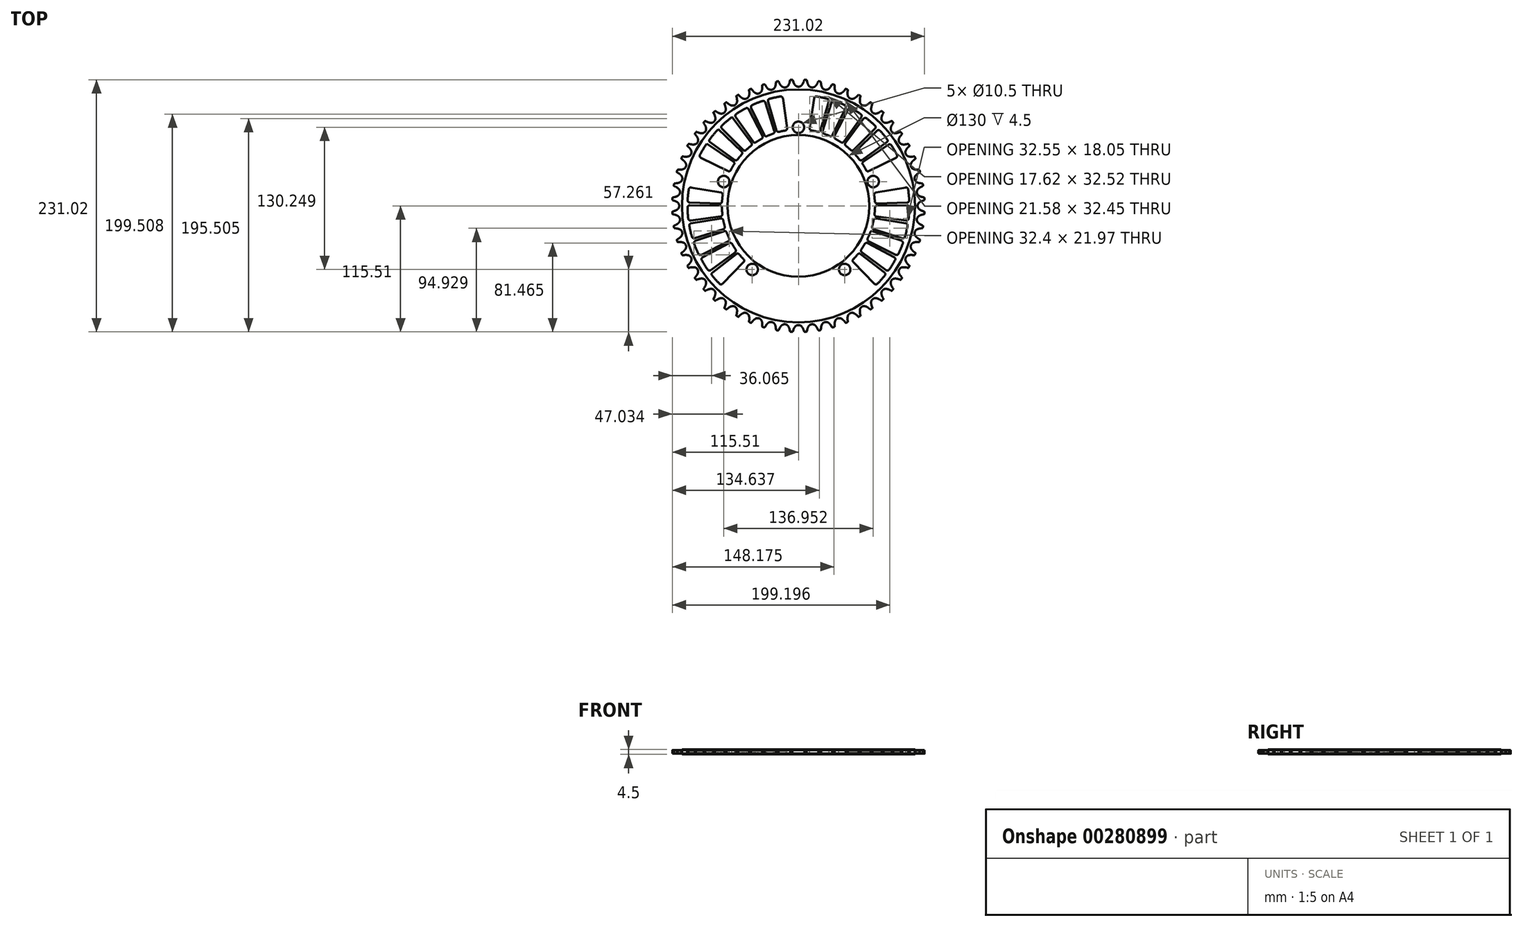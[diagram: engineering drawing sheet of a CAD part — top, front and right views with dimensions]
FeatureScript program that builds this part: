
annotation { "Feature Type Name" : "Feature", "Feature Type Description" : "" }
export const myFeature = defineFeature(function(context is Context, id is Id, definition is map)
    precondition{}
    {
        {
            var Q0;
            Q0=qCreatedBy(makeId("Top.planeOp"),FACE);
            var sketch = newSketch(context, id + "F0", { "sketchPlane" : qUnion([Q0])});
            skArc(sketch, "E0", {"start": v(-3.25, 110.83) * mm, "mid": v(-1.82, 109.61) * mm, "end": v(0, 109.18) * mm});
            skArc(sketch, "E1", {"start": v(-4.68, 113.54) * mm, "mid": v(-4.06, 112.13) * mm, "end": v(-3.25, 110.83) * mm});
            skLineSegment(sketch, "E2", {"start": v(-4.68, 113.54) * mm, "end": v(-5.07, 114.66) * mm});
            skLineSegment(sketch, "E3", {"start": v(-11.11, 112.64) * mm, "end": v(-11.11, 112.57) * mm});
            skArc(sketch, "E4.trimOffspring", {"start": v(-5.07, 114.66) * mm, "mid": v(-5.69, 115.95) * mm, "end": v(-6.57, 117.07) * mm});
            skArc(sketch, "E5.MirrorCS", {"start": v(3.25, 110.83) * mm, "mid": v(1.82, 109.61) * mm, "end": v(0, 109.18) * mm});
            skArc(sketch, "E6.MirrorCS", {"start": v(4.68, 113.54) * mm, "mid": v(4.06, 112.13) * mm, "end": v(3.25, 110.83) * mm});
            skLineSegment(sketch, "E7.MirrorCS", {"start": v(4.68, 113.54) * mm, "end": v(5.07, 114.66) * mm});
            skArc(sketch, "E8.MirrorCS", {"start": v(5.07, 114.66) * mm, "mid": v(5.69, 115.95) * mm, "end": v(6.57, 117.07) * mm});
            skArc(sketch, "E9.1.0", {"start": v(-17.87, 113.37) * mm, "mid": v(-18.63, 114.58) * mm, "end": v(-19.64, 115.6) * mm});
            skLineSegment(sketch, "E9.1.1", {"start": v(-17.36, 112.3) * mm, "end": v(-17.87, 113.37) * mm});
            skArc(sketch, "E9.1.2", {"start": v(-17.36, 112.3) * mm, "mid": v(-16.6, 110.97) * mm, "end": v(-15.63, 109.77) * mm});
            skArc(sketch, "E9.1.3", {"start": v(-15.63, 109.77) * mm, "mid": v(-14.08, 108.72) * mm, "end": v(-12.22, 108.49) * mm});
            skArc(sketch, "E9.1.4", {"start": v(-9.18, 110.5) * mm, "mid": v(-10.46, 109.13) * mm, "end": v(-12.22, 108.49) * mm});
            skArc(sketch, "E9.1.5", {"start": v(-8.06, 113.35) * mm, "mid": v(-8.52, 111.88) * mm, "end": v(-9.18, 110.5) * mm});
            skLineSegment(sketch, "E9.1.6", {"start": v(-8.06, 113.35) * mm, "end": v(-7.8, 114.5) * mm});
            skArc(sketch, "E9.1.7", {"start": v(-7.8, 114.5) * mm, "mid": v(-7.33, 115.86) * mm, "end": v(-6.57, 117.07) * mm});
            skArc(sketch, "E9.2.0", {"start": v(-30.45, 110.65) * mm, "mid": v(-31.34, 111.78) * mm, "end": v(-32.46, 112.68) * mm});
            skLineSegment(sketch, "E9.2.1", {"start": v(-29.83, 109.65) * mm, "end": v(-30.45, 110.65) * mm});
            skArc(sketch, "E9.2.2", {"start": v(-29.83, 109.65) * mm, "mid": v(-28.91, 108.41) * mm, "end": v(-27.83, 107.33) * mm});
            skArc(sketch, "E9.2.3", {"start": v(-27.83, 107.33) * mm, "mid": v(-26.17, 106.46) * mm, "end": v(-24.3, 106.44) * mm});
            skArc(sketch, "E9.2.4", {"start": v(-21.5, 108.77) * mm, "mid": v(-22.62, 107.27) * mm, "end": v(-24.3, 106.44) * mm});
            skArc(sketch, "E9.2.5", {"start": v(-20.7, 111.74) * mm, "mid": v(-20.99, 110.22) * mm, "end": v(-21.5, 108.77) * mm});
            skLineSegment(sketch, "E9.2.6", {"start": v(-20.7, 111.74) * mm, "end": v(-20.57, 112.9) * mm});
            skArc(sketch, "E9.2.7", {"start": v(-20.57, 112.9) * mm, "mid": v(-20.26, 114.3) * mm, "end": v(-19.64, 115.6) * mm});
            skArc(sketch, "E9.3.0", {"start": v(-42.65, 106.55) * mm, "mid": v(-43.66, 107.57) * mm, "end": v(-44.87, 108.33) * mm});
            skLineSegment(sketch, "E9.3.1", {"start": v(-41.92, 105.62) * mm, "end": v(-42.65, 106.55) * mm});
            skArc(sketch, "E9.3.2", {"start": v(-41.92, 105.62) * mm, "mid": v(-40.87, 104.5) * mm, "end": v(-39.67, 103.54) * mm});
            skArc(sketch, "E9.3.3", {"start": v(-39.67, 103.54) * mm, "mid": v(-37.92, 102.86) * mm, "end": v(-36.06, 103.05) * mm});
            skArc(sketch, "E9.3.4", {"start": v(-33.54, 105.68) * mm, "mid": v(-34.48, 104.06) * mm, "end": v(-36.06, 103.05) * mm});
            skArc(sketch, "E9.3.5", {"start": v(-33.08, 108.71) * mm, "mid": v(-33.2, 107.18) * mm, "end": v(-33.54, 105.68) * mm});
            skLineSegment(sketch, "E9.3.6", {"start": v(-33.08, 108.71) * mm, "end": v(-33.09, 109.9) * mm});
            skArc(sketch, "E9.3.7", {"start": v(-33.09, 109.9) * mm, "mid": v(-32.93, 111.32) * mm, "end": v(-32.46, 112.68) * mm});
            skArc(sketch, "E9.4.0", {"start": v(-54.31, 101.1) * mm, "mid": v(-55.43, 102) * mm, "end": v(-56.72, 102.63) * mm});
            skLineSegment(sketch, "E9.4.1", {"start": v(-53.48, 100.26) * mm, "end": v(-54.31, 101.1) * mm});
            skArc(sketch, "E9.4.2", {"start": v(-53.48, 100.26) * mm, "mid": v(-52.31, 99.26) * mm, "end": v(-51, 98.44) * mm});
            skArc(sketch, "E9.4.3", {"start": v(-51, 98.44) * mm, "mid": v(-49.2, 97.97) * mm, "end": v(-47.37, 98.36) * mm});
            skArc(sketch, "E9.4.4", {"start": v(-45.16, 101.26) * mm, "mid": v(-45.92, 99.55) * mm, "end": v(-47.37, 98.36) * mm});
            skArc(sketch, "E9.4.5", {"start": v(-45.04, 104.33) * mm, "mid": v(-44.99, 102.79) * mm, "end": v(-45.16, 101.26) * mm});
            skLineSegment(sketch, "E9.4.6", {"start": v(-45.04, 104.33) * mm, "end": v(-45.18, 105.5) * mm});
            skArc(sketch, "E9.4.7", {"start": v(-45.18, 105.5) * mm, "mid": v(-45.19, 106.93) * mm, "end": v(-44.87, 108.33) * mm});
            skArc(sketch, "E9.5.0", {"start": v(-65.3, 94.39) * mm, "mid": v(-66.5, 95.15) * mm, "end": v(-67.85, 95.63) * mm});
            skLineSegment(sketch, "E9.5.1", {"start": v(-64.37, 93.65) * mm, "end": v(-65.3, 94.39) * mm});
            skArc(sketch, "E9.5.2", {"start": v(-64.37, 93.65) * mm, "mid": v(-63.1, 92.78) * mm, "end": v(-61.71, 92.11) * mm});
            skArc(sketch, "E9.5.3", {"start": v(-61.71, 92.11) * mm, "mid": v(-59.86, 91.84) * mm, "end": v(-58.09, 92.44) * mm});
            skArc(sketch, "E9.5.4", {"start": v(-56.22, 95.57) * mm, "mid": v(-56.78, 93.78) * mm, "end": v(-58.09, 92.44) * mm});
            skArc(sketch, "E9.5.5", {"start": v(-56.44, 98.63) * mm, "mid": v(-56.22, 97.1) * mm, "end": v(-56.22, 95.57) * mm});
            skLineSegment(sketch, "E9.5.6", {"start": v(-56.44, 98.63) * mm, "end": v(-56.7, 99.78) * mm});
            skArc(sketch, "E9.5.7", {"start": v(-56.7, 99.78) * mm, "mid": v(-56.88, 101.2) * mm, "end": v(-56.72, 102.63) * mm});
            skArc(sketch, "E9.6.0", {"start": v(-75.45, 86.48) * mm, "mid": v(-76.74, 87.1) * mm, "end": v(-78.13, 87.43) * mm});
            skLineSegment(sketch, "E9.6.1", {"start": v(-74.45, 85.85) * mm, "end": v(-75.45, 86.48) * mm});
            skArc(sketch, "E9.6.2", {"start": v(-74.45, 85.85) * mm, "mid": v(-73.09, 85.13) * mm, "end": v(-71.64, 84.62) * mm});
            skArc(sketch, "E9.6.3", {"start": v(-71.64, 84.62) * mm, "mid": v(-69.77, 84.56) * mm, "end": v(-68.07, 85.36) * mm});
            skArc(sketch, "E9.6.4", {"start": v(-66.56, 88.67) * mm, "mid": v(-66.92, 86.83) * mm, "end": v(-68.07, 85.36) * mm});
            skArc(sketch, "E9.6.5", {"start": v(-67.13, 91.69) * mm, "mid": v(-66.73, 90.2) * mm, "end": v(-66.56, 88.67) * mm});
            skLineSegment(sketch, "E9.6.6", {"start": v(-67.13, 91.69) * mm, "end": v(-67.52, 92.8) * mm});
            skArc(sketch, "E9.6.7", {"start": v(-67.52, 92.8) * mm, "mid": v(-67.85, 94.2) * mm, "end": v(-67.85, 95.63) * mm});
            skArc(sketch, "E9.7.0", {"start": v(-84.66, 77.5) * mm, "mid": v(-86, 77.97) * mm, "end": v(-87.43, 78.13) * mm});
            skLineSegment(sketch, "E9.7.1", {"start": v(-83.6, 76.97) * mm, "end": v(-84.66, 77.5) * mm});
            skArc(sketch, "E9.7.2", {"start": v(-83.6, 76.97) * mm, "mid": v(-82.16, 76.41) * mm, "end": v(-80.66, 76.07) * mm});
            skArc(sketch, "E9.7.3", {"start": v(-80.66, 76.07) * mm, "mid": v(-78.8, 76.22) * mm, "end": v(-77.2, 77.2) * mm});
            skArc(sketch, "E9.7.4", {"start": v(-76.07, 80.66) * mm, "mid": v(-76.22, 78.8) * mm, "end": v(-77.2, 77.2) * mm});
            skArc(sketch, "E9.7.5", {"start": v(-76.97, 83.6) * mm, "mid": v(-76.41, 82.16) * mm, "end": v(-76.07, 80.66) * mm});
            skLineSegment(sketch, "E9.7.6", {"start": v(-76.97, 83.6) * mm, "end": v(-77.5, 84.66) * mm});
            skArc(sketch, "E9.7.7", {"start": v(-77.5, 84.66) * mm, "mid": v(-77.97, 86) * mm, "end": v(-78.13, 87.43) * mm});
            skArc(sketch, "E9.8.0", {"start": v(-92.8, 67.52) * mm, "mid": v(-94.2, 67.85) * mm, "end": v(-95.63, 67.85) * mm});
            skLineSegment(sketch, "E9.8.1", {"start": v(-91.69, 67.13) * mm, "end": v(-92.8, 67.52) * mm});
            skArc(sketch, "E9.8.2", {"start": v(-91.69, 67.13) * mm, "mid": v(-90.2, 66.73) * mm, "end": v(-88.67, 66.56) * mm});
            skArc(sketch, "E9.8.3", {"start": v(-88.67, 66.56) * mm, "mid": v(-86.83, 66.92) * mm, "end": v(-85.36, 68.07) * mm});
            skArc(sketch, "E9.8.4", {"start": v(-84.62, 71.64) * mm, "mid": v(-84.56, 69.77) * mm, "end": v(-85.36, 68.07) * mm});
            skArc(sketch, "E9.8.5", {"start": v(-85.85, 74.45) * mm, "mid": v(-85.13, 73.09) * mm, "end": v(-84.62, 71.64) * mm});
            skLineSegment(sketch, "E9.8.6", {"start": v(-85.85, 74.45) * mm, "end": v(-86.48, 75.45) * mm});
            skArc(sketch, "E9.8.7", {"start": v(-86.48, 75.45) * mm, "mid": v(-87.1, 76.74) * mm, "end": v(-87.43, 78.13) * mm});
            skArc(sketch, "E9.9.0", {"start": v(-99.78, 56.7) * mm, "mid": v(-101.2, 56.88) * mm, "end": v(-102.63, 56.72) * mm});
            skLineSegment(sketch, "E9.9.1", {"start": v(-98.63, 56.44) * mm, "end": v(-99.78, 56.7) * mm});
            skArc(sketch, "E9.9.2", {"start": v(-98.63, 56.44) * mm, "mid": v(-97.1, 56.22) * mm, "end": v(-95.57, 56.22) * mm});
            skArc(sketch, "E9.9.3", {"start": v(-95.57, 56.22) * mm, "mid": v(-93.78, 56.78) * mm, "end": v(-92.44, 58.09) * mm});
            skArc(sketch, "E9.9.4", {"start": v(-92.11, 61.71) * mm, "mid": v(-91.84, 59.86) * mm, "end": v(-92.44, 58.09) * mm});
            skArc(sketch, "E9.9.5", {"start": v(-93.65, 64.37) * mm, "mid": v(-92.78, 63.1) * mm, "end": v(-92.11, 61.71) * mm});
            skLineSegment(sketch, "E9.9.6", {"start": v(-93.65, 64.37) * mm, "end": v(-94.39, 65.3) * mm});
            skArc(sketch, "E9.9.7", {"start": v(-94.39, 65.3) * mm, "mid": v(-95.15, 66.5) * mm, "end": v(-95.63, 67.85) * mm});
            skArc(sketch, "E9.10.0", {"start": v(-105.5, 45.18) * mm, "mid": v(-106.93, 45.19) * mm, "end": v(-108.33, 44.87) * mm});
            skLineSegment(sketch, "E9.10.1", {"start": v(-104.33, 45.04) * mm, "end": v(-105.5, 45.18) * mm});
            skArc(sketch, "E9.10.2", {"start": v(-104.33, 45.04) * mm, "mid": v(-102.79, 44.99) * mm, "end": v(-101.26, 45.16) * mm});
            skArc(sketch, "E9.10.3", {"start": v(-101.26, 45.16) * mm, "mid": v(-99.55, 45.92) * mm, "end": v(-98.36, 47.37) * mm});
            skArc(sketch, "E9.10.4", {"start": v(-98.44, 51) * mm, "mid": v(-97.97, 49.2) * mm, "end": v(-98.36, 47.37) * mm});
            skArc(sketch, "E9.10.5", {"start": v(-100.26, 53.48) * mm, "mid": v(-99.26, 52.31) * mm, "end": v(-98.44, 51) * mm});
            skLineSegment(sketch, "E9.10.6", {"start": v(-100.26, 53.48) * mm, "end": v(-101.1, 54.31) * mm});
            skArc(sketch, "E9.10.7", {"start": v(-101.1, 54.31) * mm, "mid": v(-102, 55.43) * mm, "end": v(-102.63, 56.72) * mm});
            skArc(sketch, "E9.11.0", {"start": v(-109.9, 33.09) * mm, "mid": v(-111.32, 32.93) * mm, "end": v(-112.68, 32.46) * mm});
            skLineSegment(sketch, "E9.11.1", {"start": v(-108.71, 33.08) * mm, "end": v(-109.9, 33.09) * mm});
            skArc(sketch, "E9.11.2", {"start": v(-108.71, 33.08) * mm, "mid": v(-107.18, 33.2) * mm, "end": v(-105.68, 33.54) * mm});
            skArc(sketch, "E9.11.3", {"start": v(-105.68, 33.54) * mm, "mid": v(-104.06, 34.48) * mm, "end": v(-103.05, 36.06) * mm});
            skArc(sketch, "E9.11.4", {"start": v(-103.54, 39.67) * mm, "mid": v(-102.86, 37.92) * mm, "end": v(-103.05, 36.06) * mm});
            skArc(sketch, "E9.11.5", {"start": v(-105.62, 41.92) * mm, "mid": v(-104.5, 40.87) * mm, "end": v(-103.54, 39.67) * mm});
            skLineSegment(sketch, "E9.11.6", {"start": v(-105.62, 41.92) * mm, "end": v(-106.55, 42.65) * mm});
            skArc(sketch, "E9.11.7", {"start": v(-106.55, 42.65) * mm, "mid": v(-107.57, 43.66) * mm, "end": v(-108.33, 44.87) * mm});
            skArc(sketch, "E9.12.0", {"start": v(-112.9, 20.57) * mm, "mid": v(-114.3, 20.26) * mm, "end": v(-115.6, 19.64) * mm});
            skLineSegment(sketch, "E9.12.1", {"start": v(-111.74, 20.7) * mm, "end": v(-112.9, 20.57) * mm});
            skArc(sketch, "E9.12.2", {"start": v(-111.74, 20.7) * mm, "mid": v(-110.22, 20.99) * mm, "end": v(-108.77, 21.5) * mm});
            skArc(sketch, "E9.12.3", {"start": v(-108.77, 21.5) * mm, "mid": v(-107.27, 22.62) * mm, "end": v(-106.44, 24.3) * mm});
            skArc(sketch, "E9.12.4", {"start": v(-107.33, 27.83) * mm, "mid": v(-106.46, 26.17) * mm, "end": v(-106.44, 24.3) * mm});
            skArc(sketch, "E9.12.5", {"start": v(-109.65, 29.83) * mm, "mid": v(-108.41, 28.91) * mm, "end": v(-107.33, 27.83) * mm});
            skLineSegment(sketch, "E9.12.6", {"start": v(-109.65, 29.83) * mm, "end": v(-110.65, 30.45) * mm});
            skArc(sketch, "E9.12.7", {"start": v(-110.65, 30.45) * mm, "mid": v(-111.78, 31.34) * mm, "end": v(-112.68, 32.46) * mm});
            skArc(sketch, "E9.13.0", {"start": v(-114.5, 7.8) * mm, "mid": v(-115.86, 7.33) * mm, "end": v(-117.07, 6.57) * mm});
            skLineSegment(sketch, "E9.13.1", {"start": v(-113.35, 8.06) * mm, "end": v(-114.5, 7.8) * mm});
            skArc(sketch, "E9.13.2", {"start": v(-113.35, 8.06) * mm, "mid": v(-111.88, 8.52) * mm, "end": v(-110.5, 9.18) * mm});
            skArc(sketch, "E9.13.3", {"start": v(-110.5, 9.18) * mm, "mid": v(-109.13, 10.46) * mm, "end": v(-108.49, 12.22) * mm});
            skArc(sketch, "E9.13.4", {"start": v(-109.77, 15.63) * mm, "mid": v(-108.72, 14.08) * mm, "end": v(-108.49, 12.22) * mm});
            skArc(sketch, "E9.13.5", {"start": v(-112.3, 17.36) * mm, "mid": v(-110.97, 16.6) * mm, "end": v(-109.77, 15.63) * mm});
            skLineSegment(sketch, "E9.13.6", {"start": v(-112.3, 17.36) * mm, "end": v(-113.37, 17.87) * mm});
            skArc(sketch, "E9.13.7", {"start": v(-113.37, 17.87) * mm, "mid": v(-114.58, 18.63) * mm, "end": v(-115.6, 19.64) * mm});
            skArc(sketch, "E9.14.0", {"start": v(-114.66, -5.07) * mm, "mid": v(-115.95, -5.69) * mm, "end": v(-117.07, -6.57) * mm});
            skLineSegment(sketch, "E9.14.1", {"start": v(-113.54, -4.68) * mm, "end": v(-114.66, -5.07) * mm});
            skArc(sketch, "E9.14.2", {"start": v(-113.54, -4.68) * mm, "mid": v(-112.13, -4.06) * mm, "end": v(-110.83, -3.25) * mm});
            skArc(sketch, "E9.14.3", {"start": v(-110.83, -3.25) * mm, "mid": v(-109.61, -1.82) * mm, "end": v(-109.18, 0) * mm});
            skArc(sketch, "E9.14.4", {"start": v(-110.83, 3.25) * mm, "mid": v(-109.61, 1.82) * mm, "end": v(-109.18, 0) * mm});
            skArc(sketch, "E9.14.5", {"start": v(-113.54, 4.68) * mm, "mid": v(-112.13, 4.06) * mm, "end": v(-110.83, 3.25) * mm});
            skLineSegment(sketch, "E9.14.6", {"start": v(-113.54, 4.68) * mm, "end": v(-114.66, 5.07) * mm});
            skArc(sketch, "E9.14.7", {"start": v(-114.66, 5.07) * mm, "mid": v(-115.95, 5.69) * mm, "end": v(-117.07, 6.57) * mm});
            skArc(sketch, "E9.15.0", {"start": v(-113.37, -17.87) * mm, "mid": v(-114.58, -18.63) * mm, "end": v(-115.6, -19.64) * mm});
            skLineSegment(sketch, "E9.15.1", {"start": v(-112.3, -17.36) * mm, "end": v(-113.37, -17.87) * mm});
            skArc(sketch, "E9.15.2", {"start": v(-112.3, -17.36) * mm, "mid": v(-110.97, -16.6) * mm, "end": v(-109.77, -15.63) * mm});
            skArc(sketch, "E9.15.3", {"start": v(-109.77, -15.63) * mm, "mid": v(-108.72, -14.08) * mm, "end": v(-108.49, -12.22) * mm});
            skArc(sketch, "E9.15.4", {"start": v(-110.5, -9.18) * mm, "mid": v(-109.13, -10.46) * mm, "end": v(-108.49, -12.22) * mm});
            skArc(sketch, "E9.15.5", {"start": v(-113.35, -8.06) * mm, "mid": v(-111.88, -8.52) * mm, "end": v(-110.5, -9.18) * mm});
            skLineSegment(sketch, "E9.15.6", {"start": v(-113.35, -8.06) * mm, "end": v(-114.5, -7.8) * mm});
            skArc(sketch, "E9.15.7", {"start": v(-114.5, -7.8) * mm, "mid": v(-115.86, -7.33) * mm, "end": v(-117.07, -6.57) * mm});
            skArc(sketch, "E9.16.0", {"start": v(-110.65, -30.45) * mm, "mid": v(-111.78, -31.34) * mm, "end": v(-112.68, -32.46) * mm});
            skLineSegment(sketch, "E9.16.1", {"start": v(-109.65, -29.83) * mm, "end": v(-110.65, -30.45) * mm});
            skArc(sketch, "E9.16.2", {"start": v(-109.65, -29.83) * mm, "mid": v(-108.41, -28.91) * mm, "end": v(-107.33, -27.83) * mm});
            skArc(sketch, "E9.16.3", {"start": v(-107.33, -27.83) * mm, "mid": v(-106.46, -26.17) * mm, "end": v(-106.44, -24.3) * mm});
            skArc(sketch, "E9.16.4", {"start": v(-108.77, -21.5) * mm, "mid": v(-107.27, -22.62) * mm, "end": v(-106.44, -24.3) * mm});
            skArc(sketch, "E9.16.5", {"start": v(-111.74, -20.7) * mm, "mid": v(-110.22, -20.99) * mm, "end": v(-108.77, -21.5) * mm});
            skLineSegment(sketch, "E9.16.6", {"start": v(-111.74, -20.7) * mm, "end": v(-112.9, -20.57) * mm});
            skArc(sketch, "E9.16.7", {"start": v(-112.9, -20.57) * mm, "mid": v(-114.3, -20.26) * mm, "end": v(-115.6, -19.64) * mm});
            skArc(sketch, "E9.17.0", {"start": v(-106.55, -42.65) * mm, "mid": v(-107.57, -43.66) * mm, "end": v(-108.33, -44.87) * mm});
            skLineSegment(sketch, "E9.17.1", {"start": v(-105.62, -41.92) * mm, "end": v(-106.55, -42.65) * mm});
            skArc(sketch, "E9.17.2", {"start": v(-105.62, -41.92) * mm, "mid": v(-104.5, -40.87) * mm, "end": v(-103.54, -39.67) * mm});
            skArc(sketch, "E9.17.3", {"start": v(-103.54, -39.67) * mm, "mid": v(-102.86, -37.92) * mm, "end": v(-103.05, -36.06) * mm});
            skArc(sketch, "E9.17.4", {"start": v(-105.68, -33.54) * mm, "mid": v(-104.06, -34.48) * mm, "end": v(-103.05, -36.06) * mm});
            skArc(sketch, "E9.17.5", {"start": v(-108.71, -33.08) * mm, "mid": v(-107.18, -33.2) * mm, "end": v(-105.68, -33.54) * mm});
            skLineSegment(sketch, "E9.17.6", {"start": v(-108.71, -33.08) * mm, "end": v(-109.9, -33.09) * mm});
            skArc(sketch, "E9.17.7", {"start": v(-109.9, -33.09) * mm, "mid": v(-111.32, -32.93) * mm, "end": v(-112.68, -32.46) * mm});
            skArc(sketch, "E9.18.0", {"start": v(-101.1, -54.31) * mm, "mid": v(-102, -55.43) * mm, "end": v(-102.63, -56.72) * mm});
            skLineSegment(sketch, "E9.18.1", {"start": v(-100.26, -53.48) * mm, "end": v(-101.1, -54.31) * mm});
            skArc(sketch, "E9.18.2", {"start": v(-100.26, -53.48) * mm, "mid": v(-99.26, -52.31) * mm, "end": v(-98.44, -51) * mm});
            skArc(sketch, "E9.18.3", {"start": v(-98.44, -51) * mm, "mid": v(-97.97, -49.2) * mm, "end": v(-98.36, -47.37) * mm});
            skArc(sketch, "E9.18.4", {"start": v(-101.26, -45.16) * mm, "mid": v(-99.55, -45.92) * mm, "end": v(-98.36, -47.37) * mm});
            skArc(sketch, "E9.18.5", {"start": v(-104.33, -45.04) * mm, "mid": v(-102.79, -44.99) * mm, "end": v(-101.26, -45.16) * mm});
            skLineSegment(sketch, "E9.18.6", {"start": v(-104.33, -45.04) * mm, "end": v(-105.5, -45.18) * mm});
            skArc(sketch, "E9.18.7", {"start": v(-105.5, -45.18) * mm, "mid": v(-106.93, -45.19) * mm, "end": v(-108.33, -44.87) * mm});
            skArc(sketch, "E9.19.0", {"start": v(-94.39, -65.3) * mm, "mid": v(-95.15, -66.5) * mm, "end": v(-95.63, -67.85) * mm});
            skLineSegment(sketch, "E9.19.1", {"start": v(-93.65, -64.37) * mm, "end": v(-94.39, -65.3) * mm});
            skArc(sketch, "E9.19.2", {"start": v(-93.65, -64.37) * mm, "mid": v(-92.78, -63.1) * mm, "end": v(-92.11, -61.71) * mm});
            skArc(sketch, "E9.19.3", {"start": v(-92.11, -61.71) * mm, "mid": v(-91.84, -59.86) * mm, "end": v(-92.44, -58.09) * mm});
            skArc(sketch, "E9.19.4", {"start": v(-95.57, -56.22) * mm, "mid": v(-93.78, -56.78) * mm, "end": v(-92.44, -58.09) * mm});
            skArc(sketch, "E9.19.5", {"start": v(-98.63, -56.44) * mm, "mid": v(-97.1, -56.22) * mm, "end": v(-95.57, -56.22) * mm});
            skLineSegment(sketch, "E9.19.6", {"start": v(-98.63, -56.44) * mm, "end": v(-99.78, -56.7) * mm});
            skArc(sketch, "E9.19.7", {"start": v(-99.78, -56.7) * mm, "mid": v(-101.2, -56.88) * mm, "end": v(-102.63, -56.72) * mm});
            skArc(sketch, "E9.20.0", {"start": v(-86.48, -75.45) * mm, "mid": v(-87.1, -76.74) * mm, "end": v(-87.43, -78.13) * mm});
            skLineSegment(sketch, "E9.20.1", {"start": v(-85.85, -74.45) * mm, "end": v(-86.48, -75.45) * mm});
            skArc(sketch, "E9.20.2", {"start": v(-85.85, -74.45) * mm, "mid": v(-85.13, -73.09) * mm, "end": v(-84.62, -71.64) * mm});
            skArc(sketch, "E9.20.3", {"start": v(-84.62, -71.64) * mm, "mid": v(-84.56, -69.77) * mm, "end": v(-85.36, -68.07) * mm});
            skArc(sketch, "E9.20.4", {"start": v(-88.67, -66.56) * mm, "mid": v(-86.83, -66.92) * mm, "end": v(-85.36, -68.07) * mm});
            skArc(sketch, "E9.20.5", {"start": v(-91.69, -67.13) * mm, "mid": v(-90.2, -66.73) * mm, "end": v(-88.67, -66.56) * mm});
            skLineSegment(sketch, "E9.20.6", {"start": v(-91.69, -67.13) * mm, "end": v(-92.8, -67.52) * mm});
            skArc(sketch, "E9.20.7", {"start": v(-92.8, -67.52) * mm, "mid": v(-94.2, -67.85) * mm, "end": v(-95.63, -67.85) * mm});
            skArc(sketch, "E9.21.0", {"start": v(-77.5, -84.66) * mm, "mid": v(-77.97, -86) * mm, "end": v(-78.13, -87.43) * mm});
            skLineSegment(sketch, "E9.21.1", {"start": v(-76.97, -83.6) * mm, "end": v(-77.5, -84.66) * mm});
            skArc(sketch, "E9.21.2", {"start": v(-76.97, -83.6) * mm, "mid": v(-76.41, -82.16) * mm, "end": v(-76.07, -80.66) * mm});
            skArc(sketch, "E9.21.3", {"start": v(-76.07, -80.66) * mm, "mid": v(-76.22, -78.8) * mm, "end": v(-77.2, -77.2) * mm});
            skArc(sketch, "E9.21.4", {"start": v(-80.66, -76.07) * mm, "mid": v(-78.8, -76.22) * mm, "end": v(-77.2, -77.2) * mm});
            skArc(sketch, "E9.21.5", {"start": v(-83.6, -76.97) * mm, "mid": v(-82.16, -76.41) * mm, "end": v(-80.66, -76.07) * mm});
            skLineSegment(sketch, "E9.21.6", {"start": v(-83.6, -76.97) * mm, "end": v(-84.66, -77.5) * mm});
            skArc(sketch, "E9.21.7", {"start": v(-84.66, -77.5) * mm, "mid": v(-86, -77.97) * mm, "end": v(-87.43, -78.13) * mm});
            skArc(sketch, "E9.22.0", {"start": v(-67.52, -92.8) * mm, "mid": v(-67.85, -94.2) * mm, "end": v(-67.85, -95.63) * mm});
            skLineSegment(sketch, "E9.22.1", {"start": v(-67.13, -91.69) * mm, "end": v(-67.52, -92.8) * mm});
            skArc(sketch, "E9.22.2", {"start": v(-67.13, -91.69) * mm, "mid": v(-66.73, -90.2) * mm, "end": v(-66.56, -88.67) * mm});
            skArc(sketch, "E9.22.3", {"start": v(-66.56, -88.67) * mm, "mid": v(-66.92, -86.83) * mm, "end": v(-68.07, -85.36) * mm});
            skArc(sketch, "E9.22.4", {"start": v(-71.64, -84.62) * mm, "mid": v(-69.77, -84.56) * mm, "end": v(-68.07, -85.36) * mm});
            skArc(sketch, "E9.22.5", {"start": v(-74.45, -85.85) * mm, "mid": v(-73.09, -85.13) * mm, "end": v(-71.64, -84.62) * mm});
            skLineSegment(sketch, "E9.22.6", {"start": v(-74.45, -85.85) * mm, "end": v(-75.45, -86.48) * mm});
            skArc(sketch, "E9.22.7", {"start": v(-75.45, -86.48) * mm, "mid": v(-76.74, -87.1) * mm, "end": v(-78.13, -87.43) * mm});
            skArc(sketch, "E9.23.0", {"start": v(-56.7, -99.78) * mm, "mid": v(-56.88, -101.2) * mm, "end": v(-56.72, -102.63) * mm});
            skLineSegment(sketch, "E9.23.1", {"start": v(-56.44, -98.63) * mm, "end": v(-56.7, -99.78) * mm});
            skArc(sketch, "E9.23.2", {"start": v(-56.44, -98.63) * mm, "mid": v(-56.22, -97.1) * mm, "end": v(-56.22, -95.57) * mm});
            skArc(sketch, "E9.23.3", {"start": v(-56.22, -95.57) * mm, "mid": v(-56.78, -93.78) * mm, "end": v(-58.09, -92.44) * mm});
            skArc(sketch, "E9.23.4", {"start": v(-61.71, -92.11) * mm, "mid": v(-59.86, -91.84) * mm, "end": v(-58.09, -92.44) * mm});
            skArc(sketch, "E9.23.5", {"start": v(-64.37, -93.65) * mm, "mid": v(-63.1, -92.78) * mm, "end": v(-61.71, -92.11) * mm});
            skLineSegment(sketch, "E9.23.6", {"start": v(-64.37, -93.65) * mm, "end": v(-65.3, -94.39) * mm});
            skArc(sketch, "E9.23.7", {"start": v(-65.3, -94.39) * mm, "mid": v(-66.5, -95.15) * mm, "end": v(-67.85, -95.63) * mm});
            skArc(sketch, "E9.24.0", {"start": v(-45.18, -105.5) * mm, "mid": v(-45.19, -106.93) * mm, "end": v(-44.87, -108.33) * mm});
            skLineSegment(sketch, "E9.24.1", {"start": v(-45.04, -104.33) * mm, "end": v(-45.18, -105.5) * mm});
            skArc(sketch, "E9.24.2", {"start": v(-45.04, -104.33) * mm, "mid": v(-44.99, -102.79) * mm, "end": v(-45.16, -101.26) * mm});
            skArc(sketch, "E9.24.3", {"start": v(-45.16, -101.26) * mm, "mid": v(-45.92, -99.55) * mm, "end": v(-47.37, -98.36) * mm});
            skArc(sketch, "E9.24.4", {"start": v(-51, -98.44) * mm, "mid": v(-49.2, -97.97) * mm, "end": v(-47.37, -98.36) * mm});
            skArc(sketch, "E9.24.5", {"start": v(-53.48, -100.26) * mm, "mid": v(-52.31, -99.26) * mm, "end": v(-51, -98.44) * mm});
            skLineSegment(sketch, "E9.24.6", {"start": v(-53.48, -100.26) * mm, "end": v(-54.31, -101.1) * mm});
            skArc(sketch, "E9.24.7", {"start": v(-54.31, -101.1) * mm, "mid": v(-55.43, -102) * mm, "end": v(-56.72, -102.63) * mm});
            skArc(sketch, "E9.25.0", {"start": v(-33.09, -109.9) * mm, "mid": v(-32.93, -111.32) * mm, "end": v(-32.46, -112.68) * mm});
            skLineSegment(sketch, "E9.25.1", {"start": v(-33.08, -108.71) * mm, "end": v(-33.09, -109.9) * mm});
            skArc(sketch, "E9.25.2", {"start": v(-33.08, -108.71) * mm, "mid": v(-33.2, -107.18) * mm, "end": v(-33.54, -105.68) * mm});
            skArc(sketch, "E9.25.3", {"start": v(-33.54, -105.68) * mm, "mid": v(-34.48, -104.06) * mm, "end": v(-36.06, -103.05) * mm});
            skArc(sketch, "E9.25.4", {"start": v(-39.67, -103.54) * mm, "mid": v(-37.92, -102.86) * mm, "end": v(-36.06, -103.05) * mm});
            skArc(sketch, "E9.25.5", {"start": v(-41.92, -105.62) * mm, "mid": v(-40.87, -104.5) * mm, "end": v(-39.67, -103.54) * mm});
            skLineSegment(sketch, "E9.25.6", {"start": v(-41.92, -105.62) * mm, "end": v(-42.65, -106.55) * mm});
            skArc(sketch, "E9.25.7", {"start": v(-42.65, -106.55) * mm, "mid": v(-43.66, -107.57) * mm, "end": v(-44.87, -108.33) * mm});
            skArc(sketch, "E9.26.0", {"start": v(-20.57, -112.9) * mm, "mid": v(-20.26, -114.3) * mm, "end": v(-19.64, -115.6) * mm});
            skLineSegment(sketch, "E9.26.1", {"start": v(-20.7, -111.74) * mm, "end": v(-20.57, -112.9) * mm});
            skArc(sketch, "E9.26.2", {"start": v(-20.7, -111.74) * mm, "mid": v(-20.99, -110.22) * mm, "end": v(-21.5, -108.77) * mm});
            skArc(sketch, "E9.26.3", {"start": v(-21.5, -108.77) * mm, "mid": v(-22.62, -107.27) * mm, "end": v(-24.3, -106.44) * mm});
            skArc(sketch, "E9.26.4", {"start": v(-27.83, -107.33) * mm, "mid": v(-26.17, -106.46) * mm, "end": v(-24.3, -106.44) * mm});
            skArc(sketch, "E9.26.5", {"start": v(-29.83, -109.65) * mm, "mid": v(-28.91, -108.41) * mm, "end": v(-27.83, -107.33) * mm});
            skLineSegment(sketch, "E9.26.6", {"start": v(-29.83, -109.65) * mm, "end": v(-30.45, -110.65) * mm});
            skArc(sketch, "E9.26.7", {"start": v(-30.45, -110.65) * mm, "mid": v(-31.34, -111.78) * mm, "end": v(-32.46, -112.68) * mm});
            skArc(sketch, "E9.27.0", {"start": v(-7.8, -114.5) * mm, "mid": v(-7.33, -115.86) * mm, "end": v(-6.57, -117.07) * mm});
            skLineSegment(sketch, "E9.27.1", {"start": v(-8.06, -113.35) * mm, "end": v(-7.8, -114.5) * mm});
            skArc(sketch, "E9.27.2", {"start": v(-8.06, -113.35) * mm, "mid": v(-8.52, -111.88) * mm, "end": v(-9.18, -110.5) * mm});
            skArc(sketch, "E9.27.3", {"start": v(-9.18, -110.5) * mm, "mid": v(-10.46, -109.13) * mm, "end": v(-12.22, -108.49) * mm});
            skArc(sketch, "E9.27.4", {"start": v(-15.63, -109.77) * mm, "mid": v(-14.08, -108.72) * mm, "end": v(-12.22, -108.49) * mm});
            skArc(sketch, "E9.27.5", {"start": v(-17.36, -112.3) * mm, "mid": v(-16.6, -110.97) * mm, "end": v(-15.63, -109.77) * mm});
            skLineSegment(sketch, "E9.27.6", {"start": v(-17.36, -112.3) * mm, "end": v(-17.87, -113.37) * mm});
            skArc(sketch, "E9.27.7", {"start": v(-17.87, -113.37) * mm, "mid": v(-18.63, -114.58) * mm, "end": v(-19.64, -115.6) * mm});
            skArc(sketch, "E9.28.0", {"start": v(5.07, -114.66) * mm, "mid": v(5.69, -115.95) * mm, "end": v(6.57, -117.07) * mm});
            skLineSegment(sketch, "E9.28.1", {"start": v(4.68, -113.54) * mm, "end": v(5.07, -114.66) * mm});
            skArc(sketch, "E9.28.2", {"start": v(4.68, -113.54) * mm, "mid": v(4.06, -112.13) * mm, "end": v(3.25, -110.83) * mm});
            skArc(sketch, "E9.28.3", {"start": v(3.25, -110.83) * mm, "mid": v(1.82, -109.61) * mm, "end": v(0, -109.18) * mm});
            skArc(sketch, "E9.28.4", {"start": v(-3.25, -110.83) * mm, "mid": v(-1.82, -109.61) * mm, "end": v(0, -109.18) * mm});
            skArc(sketch, "E9.28.5", {"start": v(-4.68, -113.54) * mm, "mid": v(-4.06, -112.13) * mm, "end": v(-3.25, -110.83) * mm});
            skLineSegment(sketch, "E9.28.6", {"start": v(-4.68, -113.54) * mm, "end": v(-5.07, -114.66) * mm});
            skArc(sketch, "E9.28.7", {"start": v(-5.07, -114.66) * mm, "mid": v(-5.69, -115.95) * mm, "end": v(-6.57, -117.07) * mm});
            skArc(sketch, "E9.29.0", {"start": v(17.87, -113.37) * mm, "mid": v(18.63, -114.58) * mm, "end": v(19.64, -115.6) * mm});
            skLineSegment(sketch, "E9.29.1", {"start": v(17.36, -112.3) * mm, "end": v(17.87, -113.37) * mm});
            skArc(sketch, "E9.29.2", {"start": v(17.36, -112.3) * mm, "mid": v(16.6, -110.97) * mm, "end": v(15.63, -109.77) * mm});
            skArc(sketch, "E9.29.3", {"start": v(15.63, -109.77) * mm, "mid": v(14.08, -108.72) * mm, "end": v(12.22, -108.49) * mm});
            skArc(sketch, "E9.29.4", {"start": v(9.18, -110.5) * mm, "mid": v(10.46, -109.13) * mm, "end": v(12.22, -108.49) * mm});
            skArc(sketch, "E9.29.5", {"start": v(8.06, -113.35) * mm, "mid": v(8.52, -111.88) * mm, "end": v(9.18, -110.5) * mm});
            skLineSegment(sketch, "E9.29.6", {"start": v(8.06, -113.35) * mm, "end": v(7.8, -114.5) * mm});
            skArc(sketch, "E9.29.7", {"start": v(7.8, -114.5) * mm, "mid": v(7.33, -115.86) * mm, "end": v(6.57, -117.07) * mm});
            skArc(sketch, "E9.30.0", {"start": v(30.45, -110.65) * mm, "mid": v(31.34, -111.78) * mm, "end": v(32.46, -112.68) * mm});
            skLineSegment(sketch, "E9.30.1", {"start": v(29.83, -109.65) * mm, "end": v(30.45, -110.65) * mm});
            skArc(sketch, "E9.30.2", {"start": v(29.83, -109.65) * mm, "mid": v(28.91, -108.41) * mm, "end": v(27.83, -107.33) * mm});
            skArc(sketch, "E9.30.3", {"start": v(27.83, -107.33) * mm, "mid": v(26.17, -106.46) * mm, "end": v(24.3, -106.44) * mm});
            skArc(sketch, "E9.30.4", {"start": v(21.5, -108.77) * mm, "mid": v(22.62, -107.27) * mm, "end": v(24.3, -106.44) * mm});
            skArc(sketch, "E9.30.5", {"start": v(20.7, -111.74) * mm, "mid": v(20.99, -110.22) * mm, "end": v(21.5, -108.77) * mm});
            skLineSegment(sketch, "E9.30.6", {"start": v(20.7, -111.74) * mm, "end": v(20.57, -112.9) * mm});
            skArc(sketch, "E9.30.7", {"start": v(20.57, -112.9) * mm, "mid": v(20.26, -114.3) * mm, "end": v(19.64, -115.6) * mm});
            skArc(sketch, "E9.31.0", {"start": v(42.65, -106.55) * mm, "mid": v(43.66, -107.57) * mm, "end": v(44.87, -108.33) * mm});
            skLineSegment(sketch, "E9.31.1", {"start": v(41.92, -105.62) * mm, "end": v(42.65, -106.55) * mm});
            skArc(sketch, "E9.31.2", {"start": v(41.92, -105.62) * mm, "mid": v(40.87, -104.5) * mm, "end": v(39.67, -103.54) * mm});
            skArc(sketch, "E9.31.3", {"start": v(39.67, -103.54) * mm, "mid": v(37.92, -102.86) * mm, "end": v(36.06, -103.05) * mm});
            skArc(sketch, "E9.31.4", {"start": v(33.54, -105.68) * mm, "mid": v(34.48, -104.06) * mm, "end": v(36.06, -103.05) * mm});
            skArc(sketch, "E9.31.5", {"start": v(33.08, -108.71) * mm, "mid": v(33.2, -107.18) * mm, "end": v(33.54, -105.68) * mm});
            skLineSegment(sketch, "E9.31.6", {"start": v(33.08, -108.71) * mm, "end": v(33.09, -109.9) * mm});
            skArc(sketch, "E9.31.7", {"start": v(33.09, -109.9) * mm, "mid": v(32.93, -111.32) * mm, "end": v(32.46, -112.68) * mm});
            skArc(sketch, "E9.32.0", {"start": v(54.31, -101.1) * mm, "mid": v(55.43, -102) * mm, "end": v(56.72, -102.63) * mm});
            skLineSegment(sketch, "E9.32.1", {"start": v(53.48, -100.26) * mm, "end": v(54.31, -101.1) * mm});
            skArc(sketch, "E9.32.2", {"start": v(53.48, -100.26) * mm, "mid": v(52.31, -99.26) * mm, "end": v(51, -98.44) * mm});
            skArc(sketch, "E9.32.3", {"start": v(51, -98.44) * mm, "mid": v(49.2, -97.97) * mm, "end": v(47.37, -98.36) * mm});
            skArc(sketch, "E9.32.4", {"start": v(45.16, -101.26) * mm, "mid": v(45.92, -99.55) * mm, "end": v(47.37, -98.36) * mm});
            skArc(sketch, "E9.32.5", {"start": v(45.04, -104.33) * mm, "mid": v(44.99, -102.79) * mm, "end": v(45.16, -101.26) * mm});
            skLineSegment(sketch, "E9.32.6", {"start": v(45.04, -104.33) * mm, "end": v(45.18, -105.5) * mm});
            skArc(sketch, "E9.32.7", {"start": v(45.18, -105.5) * mm, "mid": v(45.19, -106.93) * mm, "end": v(44.87, -108.33) * mm});
            skArc(sketch, "E9.33.0", {"start": v(65.3, -94.39) * mm, "mid": v(66.5, -95.15) * mm, "end": v(67.85, -95.63) * mm});
            skLineSegment(sketch, "E9.33.1", {"start": v(64.37, -93.65) * mm, "end": v(65.3, -94.39) * mm});
            skArc(sketch, "E9.33.2", {"start": v(64.37, -93.65) * mm, "mid": v(63.1, -92.78) * mm, "end": v(61.71, -92.11) * mm});
            skArc(sketch, "E9.33.3", {"start": v(61.71, -92.11) * mm, "mid": v(59.86, -91.84) * mm, "end": v(58.09, -92.44) * mm});
            skArc(sketch, "E9.33.4", {"start": v(56.22, -95.57) * mm, "mid": v(56.78, -93.78) * mm, "end": v(58.09, -92.44) * mm});
            skArc(sketch, "E9.33.5", {"start": v(56.44, -98.63) * mm, "mid": v(56.22, -97.1) * mm, "end": v(56.22, -95.57) * mm});
            skLineSegment(sketch, "E9.33.6", {"start": v(56.44, -98.63) * mm, "end": v(56.7, -99.78) * mm});
            skArc(sketch, "E9.33.7", {"start": v(56.7, -99.78) * mm, "mid": v(56.88, -101.2) * mm, "end": v(56.72, -102.63) * mm});
            skArc(sketch, "E9.34.0", {"start": v(75.45, -86.48) * mm, "mid": v(76.74, -87.1) * mm, "end": v(78.13, -87.43) * mm});
            skLineSegment(sketch, "E9.34.1", {"start": v(74.45, -85.85) * mm, "end": v(75.45, -86.48) * mm});
            skArc(sketch, "E9.34.2", {"start": v(74.45, -85.85) * mm, "mid": v(73.09, -85.13) * mm, "end": v(71.64, -84.62) * mm});
            skArc(sketch, "E9.34.3", {"start": v(71.64, -84.62) * mm, "mid": v(69.77, -84.56) * mm, "end": v(68.07, -85.36) * mm});
            skArc(sketch, "E9.34.4", {"start": v(66.56, -88.67) * mm, "mid": v(66.92, -86.83) * mm, "end": v(68.07, -85.36) * mm});
            skArc(sketch, "E9.34.5", {"start": v(67.13, -91.69) * mm, "mid": v(66.73, -90.2) * mm, "end": v(66.56, -88.67) * mm});
            skLineSegment(sketch, "E9.34.6", {"start": v(67.13, -91.69) * mm, "end": v(67.52, -92.8) * mm});
            skArc(sketch, "E9.34.7", {"start": v(67.52, -92.8) * mm, "mid": v(67.85, -94.2) * mm, "end": v(67.85, -95.63) * mm});
            skArc(sketch, "E9.35.0", {"start": v(84.66, -77.5) * mm, "mid": v(86, -77.97) * mm, "end": v(87.43, -78.13) * mm});
            skLineSegment(sketch, "E9.35.1", {"start": v(83.6, -76.97) * mm, "end": v(84.66, -77.5) * mm});
            skArc(sketch, "E9.35.2", {"start": v(83.6, -76.97) * mm, "mid": v(82.16, -76.41) * mm, "end": v(80.66, -76.07) * mm});
            skArc(sketch, "E9.35.3", {"start": v(80.66, -76.07) * mm, "mid": v(78.8, -76.22) * mm, "end": v(77.2, -77.2) * mm});
            skArc(sketch, "E9.35.4", {"start": v(76.07, -80.66) * mm, "mid": v(76.22, -78.8) * mm, "end": v(77.2, -77.2) * mm});
            skArc(sketch, "E9.35.5", {"start": v(76.97, -83.6) * mm, "mid": v(76.41, -82.16) * mm, "end": v(76.07, -80.66) * mm});
            skLineSegment(sketch, "E9.35.6", {"start": v(76.97, -83.6) * mm, "end": v(77.5, -84.66) * mm});
            skArc(sketch, "E9.35.7", {"start": v(77.5, -84.66) * mm, "mid": v(77.97, -86) * mm, "end": v(78.13, -87.43) * mm});
            skArc(sketch, "E9.36.0", {"start": v(92.8, -67.52) * mm, "mid": v(94.2, -67.85) * mm, "end": v(95.63, -67.85) * mm});
            skLineSegment(sketch, "E9.36.1", {"start": v(91.69, -67.13) * mm, "end": v(92.8, -67.52) * mm});
            skArc(sketch, "E9.36.2", {"start": v(91.69, -67.13) * mm, "mid": v(90.2, -66.73) * mm, "end": v(88.67, -66.56) * mm});
            skArc(sketch, "E9.36.3", {"start": v(88.67, -66.56) * mm, "mid": v(86.83, -66.92) * mm, "end": v(85.36, -68.07) * mm});
            skArc(sketch, "E9.36.4", {"start": v(84.62, -71.64) * mm, "mid": v(84.56, -69.77) * mm, "end": v(85.36, -68.07) * mm});
            skArc(sketch, "E9.36.5", {"start": v(85.85, -74.45) * mm, "mid": v(85.13, -73.09) * mm, "end": v(84.62, -71.64) * mm});
            skLineSegment(sketch, "E9.36.6", {"start": v(85.85, -74.45) * mm, "end": v(86.48, -75.45) * mm});
            skArc(sketch, "E9.36.7", {"start": v(86.48, -75.45) * mm, "mid": v(87.1, -76.74) * mm, "end": v(87.43, -78.13) * mm});
            skArc(sketch, "E9.37.0", {"start": v(99.78, -56.7) * mm, "mid": v(101.2, -56.88) * mm, "end": v(102.63, -56.72) * mm});
            skLineSegment(sketch, "E9.37.1", {"start": v(98.63, -56.44) * mm, "end": v(99.78, -56.7) * mm});
            skArc(sketch, "E9.37.2", {"start": v(98.63, -56.44) * mm, "mid": v(97.1, -56.22) * mm, "end": v(95.57, -56.22) * mm});
            skArc(sketch, "E9.37.3", {"start": v(95.57, -56.22) * mm, "mid": v(93.78, -56.78) * mm, "end": v(92.44, -58.09) * mm});
            skArc(sketch, "E9.37.4", {"start": v(92.11, -61.71) * mm, "mid": v(91.84, -59.86) * mm, "end": v(92.44, -58.09) * mm});
            skArc(sketch, "E9.37.5", {"start": v(93.65, -64.37) * mm, "mid": v(92.78, -63.1) * mm, "end": v(92.11, -61.71) * mm});
            skLineSegment(sketch, "E9.37.6", {"start": v(93.65, -64.37) * mm, "end": v(94.39, -65.3) * mm});
            skArc(sketch, "E9.37.7", {"start": v(94.39, -65.3) * mm, "mid": v(95.15, -66.5) * mm, "end": v(95.63, -67.85) * mm});
            skArc(sketch, "E9.38.0", {"start": v(105.5, -45.18) * mm, "mid": v(106.93, -45.19) * mm, "end": v(108.33, -44.87) * mm});
            skLineSegment(sketch, "E9.38.1", {"start": v(104.33, -45.04) * mm, "end": v(105.5, -45.18) * mm});
            skArc(sketch, "E9.38.2", {"start": v(104.33, -45.04) * mm, "mid": v(102.79, -44.99) * mm, "end": v(101.26, -45.16) * mm});
            skArc(sketch, "E9.38.3", {"start": v(101.26, -45.16) * mm, "mid": v(99.55, -45.92) * mm, "end": v(98.36, -47.37) * mm});
            skArc(sketch, "E9.38.4", {"start": v(98.44, -51) * mm, "mid": v(97.97, -49.2) * mm, "end": v(98.36, -47.37) * mm});
            skArc(sketch, "E9.38.5", {"start": v(100.26, -53.48) * mm, "mid": v(99.26, -52.31) * mm, "end": v(98.44, -51) * mm});
            skLineSegment(sketch, "E9.38.6", {"start": v(100.26, -53.48) * mm, "end": v(101.1, -54.31) * mm});
            skArc(sketch, "E9.38.7", {"start": v(101.1, -54.31) * mm, "mid": v(102, -55.43) * mm, "end": v(102.63, -56.72) * mm});
            skArc(sketch, "E9.39.0", {"start": v(109.9, -33.09) * mm, "mid": v(111.32, -32.93) * mm, "end": v(112.68, -32.46) * mm});
            skLineSegment(sketch, "E9.39.1", {"start": v(108.71, -33.08) * mm, "end": v(109.9, -33.09) * mm});
            skArc(sketch, "E9.39.2", {"start": v(108.71, -33.08) * mm, "mid": v(107.18, -33.2) * mm, "end": v(105.68, -33.54) * mm});
            skArc(sketch, "E9.39.3", {"start": v(105.68, -33.54) * mm, "mid": v(104.06, -34.48) * mm, "end": v(103.05, -36.06) * mm});
            skArc(sketch, "E9.39.4", {"start": v(103.54, -39.67) * mm, "mid": v(102.86, -37.92) * mm, "end": v(103.05, -36.06) * mm});
            skArc(sketch, "E9.39.5", {"start": v(105.62, -41.92) * mm, "mid": v(104.5, -40.87) * mm, "end": v(103.54, -39.67) * mm});
            skLineSegment(sketch, "E9.39.6", {"start": v(105.62, -41.92) * mm, "end": v(106.55, -42.65) * mm});
            skArc(sketch, "E9.39.7", {"start": v(106.55, -42.65) * mm, "mid": v(107.57, -43.66) * mm, "end": v(108.33, -44.87) * mm});
            skArc(sketch, "E9.40.0", {"start": v(112.9, -20.57) * mm, "mid": v(114.3, -20.26) * mm, "end": v(115.6, -19.64) * mm});
            skLineSegment(sketch, "E9.40.1", {"start": v(111.74, -20.7) * mm, "end": v(112.9, -20.57) * mm});
            skArc(sketch, "E9.40.2", {"start": v(111.74, -20.7) * mm, "mid": v(110.22, -20.99) * mm, "end": v(108.77, -21.5) * mm});
            skArc(sketch, "E9.40.3", {"start": v(108.77, -21.5) * mm, "mid": v(107.27, -22.62) * mm, "end": v(106.44, -24.3) * mm});
            skArc(sketch, "E9.40.4", {"start": v(107.33, -27.83) * mm, "mid": v(106.46, -26.17) * mm, "end": v(106.44, -24.3) * mm});
            skArc(sketch, "E9.40.5", {"start": v(109.65, -29.83) * mm, "mid": v(108.41, -28.91) * mm, "end": v(107.33, -27.83) * mm});
            skLineSegment(sketch, "E9.40.6", {"start": v(109.65, -29.83) * mm, "end": v(110.65, -30.45) * mm});
            skArc(sketch, "E9.40.7", {"start": v(110.65, -30.45) * mm, "mid": v(111.78, -31.34) * mm, "end": v(112.68, -32.46) * mm});
            skArc(sketch, "E9.41.0", {"start": v(114.5, -7.8) * mm, "mid": v(115.86, -7.33) * mm, "end": v(117.07, -6.57) * mm});
            skLineSegment(sketch, "E9.41.1", {"start": v(113.35, -8.06) * mm, "end": v(114.5, -7.8) * mm});
            skArc(sketch, "E9.41.2", {"start": v(113.35, -8.06) * mm, "mid": v(111.88, -8.52) * mm, "end": v(110.5, -9.18) * mm});
            skArc(sketch, "E9.41.3", {"start": v(110.5, -9.18) * mm, "mid": v(109.13, -10.46) * mm, "end": v(108.49, -12.22) * mm});
            skArc(sketch, "E9.41.4", {"start": v(109.77, -15.63) * mm, "mid": v(108.72, -14.08) * mm, "end": v(108.49, -12.22) * mm});
            skArc(sketch, "E9.41.5", {"start": v(112.3, -17.36) * mm, "mid": v(110.97, -16.6) * mm, "end": v(109.77, -15.63) * mm});
            skLineSegment(sketch, "E9.41.6", {"start": v(112.3, -17.36) * mm, "end": v(113.37, -17.87) * mm});
            skArc(sketch, "E9.41.7", {"start": v(113.37, -17.87) * mm, "mid": v(114.58, -18.63) * mm, "end": v(115.6, -19.64) * mm});
            skArc(sketch, "E9.42.0", {"start": v(114.66, 5.07) * mm, "mid": v(115.95, 5.69) * mm, "end": v(117.07, 6.57) * mm});
            skLineSegment(sketch, "E9.42.1", {"start": v(113.54, 4.68) * mm, "end": v(114.66, 5.07) * mm});
            skArc(sketch, "E9.42.2", {"start": v(113.54, 4.68) * mm, "mid": v(112.13, 4.06) * mm, "end": v(110.83, 3.25) * mm});
            skArc(sketch, "E9.42.3", {"start": v(110.83, 3.25) * mm, "mid": v(109.61, 1.82) * mm, "end": v(109.18, 0) * mm});
            skArc(sketch, "E9.42.4", {"start": v(110.83, -3.25) * mm, "mid": v(109.61, -1.82) * mm, "end": v(109.18, 0) * mm});
            skArc(sketch, "E9.42.5", {"start": v(113.54, -4.68) * mm, "mid": v(112.13, -4.06) * mm, "end": v(110.83, -3.25) * mm});
            skLineSegment(sketch, "E9.42.6", {"start": v(113.54, -4.68) * mm, "end": v(114.66, -5.07) * mm});
            skArc(sketch, "E9.42.7", {"start": v(114.66, -5.07) * mm, "mid": v(115.95, -5.69) * mm, "end": v(117.07, -6.57) * mm});
            skArc(sketch, "E9.43.0", {"start": v(113.37, 17.87) * mm, "mid": v(114.58, 18.63) * mm, "end": v(115.6, 19.64) * mm});
            skLineSegment(sketch, "E9.43.1", {"start": v(112.3, 17.36) * mm, "end": v(113.37, 17.87) * mm});
            skArc(sketch, "E9.43.2", {"start": v(112.3, 17.36) * mm, "mid": v(110.97, 16.6) * mm, "end": v(109.77, 15.63) * mm});
            skArc(sketch, "E9.43.3", {"start": v(109.77, 15.63) * mm, "mid": v(108.72, 14.08) * mm, "end": v(108.49, 12.22) * mm});
            skArc(sketch, "E9.43.4", {"start": v(110.5, 9.18) * mm, "mid": v(109.13, 10.46) * mm, "end": v(108.49, 12.22) * mm});
            skArc(sketch, "E9.43.5", {"start": v(113.35, 8.06) * mm, "mid": v(111.88, 8.52) * mm, "end": v(110.5, 9.18) * mm});
            skLineSegment(sketch, "E9.43.6", {"start": v(113.35, 8.06) * mm, "end": v(114.5, 7.8) * mm});
            skArc(sketch, "E9.43.7", {"start": v(114.5, 7.8) * mm, "mid": v(115.86, 7.33) * mm, "end": v(117.07, 6.57) * mm});
            skArc(sketch, "E9.44.0", {"start": v(110.65, 30.45) * mm, "mid": v(111.78, 31.34) * mm, "end": v(112.68, 32.46) * mm});
            skLineSegment(sketch, "E9.44.1", {"start": v(109.65, 29.83) * mm, "end": v(110.65, 30.45) * mm});
            skArc(sketch, "E9.44.2", {"start": v(109.65, 29.83) * mm, "mid": v(108.41, 28.91) * mm, "end": v(107.33, 27.83) * mm});
            skArc(sketch, "E9.44.3", {"start": v(107.33, 27.83) * mm, "mid": v(106.46, 26.17) * mm, "end": v(106.44, 24.3) * mm});
            skArc(sketch, "E9.44.4", {"start": v(108.77, 21.5) * mm, "mid": v(107.27, 22.62) * mm, "end": v(106.44, 24.3) * mm});
            skArc(sketch, "E9.44.5", {"start": v(111.74, 20.7) * mm, "mid": v(110.22, 20.99) * mm, "end": v(108.77, 21.5) * mm});
            skLineSegment(sketch, "E9.44.6", {"start": v(111.74, 20.7) * mm, "end": v(112.9, 20.57) * mm});
            skArc(sketch, "E9.44.7", {"start": v(112.9, 20.57) * mm, "mid": v(114.3, 20.26) * mm, "end": v(115.6, 19.64) * mm});
            skArc(sketch, "E9.45.0", {"start": v(106.55, 42.65) * mm, "mid": v(107.57, 43.66) * mm, "end": v(108.33, 44.87) * mm});
            skLineSegment(sketch, "E9.45.1", {"start": v(105.62, 41.92) * mm, "end": v(106.55, 42.65) * mm});
            skArc(sketch, "E9.45.2", {"start": v(105.62, 41.92) * mm, "mid": v(104.5, 40.87) * mm, "end": v(103.54, 39.67) * mm});
            skArc(sketch, "E9.45.3", {"start": v(103.54, 39.67) * mm, "mid": v(102.86, 37.92) * mm, "end": v(103.05, 36.06) * mm});
            skArc(sketch, "E9.45.4", {"start": v(105.68, 33.54) * mm, "mid": v(104.06, 34.48) * mm, "end": v(103.05, 36.06) * mm});
            skArc(sketch, "E9.45.5", {"start": v(108.71, 33.08) * mm, "mid": v(107.18, 33.2) * mm, "end": v(105.68, 33.54) * mm});
            skLineSegment(sketch, "E9.45.6", {"start": v(108.71, 33.08) * mm, "end": v(109.9, 33.09) * mm});
            skArc(sketch, "E9.45.7", {"start": v(109.9, 33.09) * mm, "mid": v(111.32, 32.93) * mm, "end": v(112.68, 32.46) * mm});
            skArc(sketch, "E9.46.0", {"start": v(101.1, 54.31) * mm, "mid": v(102, 55.43) * mm, "end": v(102.63, 56.72) * mm});
            skLineSegment(sketch, "E9.46.1", {"start": v(100.26, 53.48) * mm, "end": v(101.1, 54.31) * mm});
            skArc(sketch, "E9.46.2", {"start": v(100.26, 53.48) * mm, "mid": v(99.26, 52.31) * mm, "end": v(98.44, 51) * mm});
            skArc(sketch, "E9.46.3", {"start": v(98.44, 51) * mm, "mid": v(97.97, 49.2) * mm, "end": v(98.36, 47.37) * mm});
            skArc(sketch, "E9.46.4", {"start": v(101.26, 45.16) * mm, "mid": v(99.55, 45.92) * mm, "end": v(98.36, 47.37) * mm});
            skArc(sketch, "E9.46.5", {"start": v(104.33, 45.04) * mm, "mid": v(102.79, 44.99) * mm, "end": v(101.26, 45.16) * mm});
            skLineSegment(sketch, "E9.46.6", {"start": v(104.33, 45.04) * mm, "end": v(105.5, 45.18) * mm});
            skArc(sketch, "E9.46.7", {"start": v(105.5, 45.18) * mm, "mid": v(106.93, 45.19) * mm, "end": v(108.33, 44.87) * mm});
            skArc(sketch, "E9.47.0", {"start": v(94.39, 65.3) * mm, "mid": v(95.15, 66.5) * mm, "end": v(95.63, 67.85) * mm});
            skLineSegment(sketch, "E9.47.1", {"start": v(93.65, 64.37) * mm, "end": v(94.39, 65.3) * mm});
            skArc(sketch, "E9.47.2", {"start": v(93.65, 64.37) * mm, "mid": v(92.78, 63.1) * mm, "end": v(92.11, 61.71) * mm});
            skArc(sketch, "E9.47.3", {"start": v(92.11, 61.71) * mm, "mid": v(91.84, 59.86) * mm, "end": v(92.44, 58.09) * mm});
            skArc(sketch, "E9.47.4", {"start": v(95.57, 56.22) * mm, "mid": v(93.78, 56.78) * mm, "end": v(92.44, 58.09) * mm});
            skArc(sketch, "E9.47.5", {"start": v(98.63, 56.44) * mm, "mid": v(97.1, 56.22) * mm, "end": v(95.57, 56.22) * mm});
            skLineSegment(sketch, "E9.47.6", {"start": v(98.63, 56.44) * mm, "end": v(99.78, 56.7) * mm});
            skArc(sketch, "E9.47.7", {"start": v(99.78, 56.7) * mm, "mid": v(101.2, 56.88) * mm, "end": v(102.63, 56.72) * mm});
            skArc(sketch, "E9.48.0", {"start": v(86.48, 75.45) * mm, "mid": v(87.1, 76.74) * mm, "end": v(87.43, 78.13) * mm});
            skLineSegment(sketch, "E9.48.1", {"start": v(85.85, 74.45) * mm, "end": v(86.48, 75.45) * mm});
            skArc(sketch, "E9.48.2", {"start": v(85.85, 74.45) * mm, "mid": v(85.13, 73.09) * mm, "end": v(84.62, 71.64) * mm});
            skArc(sketch, "E9.48.3", {"start": v(84.62, 71.64) * mm, "mid": v(84.56, 69.77) * mm, "end": v(85.36, 68.07) * mm});
            skArc(sketch, "E9.48.4", {"start": v(88.67, 66.56) * mm, "mid": v(86.83, 66.92) * mm, "end": v(85.36, 68.07) * mm});
            skArc(sketch, "E9.48.5", {"start": v(91.69, 67.13) * mm, "mid": v(90.2, 66.73) * mm, "end": v(88.67, 66.56) * mm});
            skLineSegment(sketch, "E9.48.6", {"start": v(91.69, 67.13) * mm, "end": v(92.8, 67.52) * mm});
            skArc(sketch, "E9.48.7", {"start": v(92.8, 67.52) * mm, "mid": v(94.2, 67.85) * mm, "end": v(95.63, 67.85) * mm});
            skArc(sketch, "E9.49.0", {"start": v(77.5, 84.66) * mm, "mid": v(77.97, 86) * mm, "end": v(78.13, 87.43) * mm});
            skLineSegment(sketch, "E9.49.1", {"start": v(76.97, 83.6) * mm, "end": v(77.5, 84.66) * mm});
            skArc(sketch, "E9.49.2", {"start": v(76.97, 83.6) * mm, "mid": v(76.41, 82.16) * mm, "end": v(76.07, 80.66) * mm});
            skArc(sketch, "E9.49.3", {"start": v(76.07, 80.66) * mm, "mid": v(76.22, 78.8) * mm, "end": v(77.2, 77.2) * mm});
            skArc(sketch, "E9.49.4", {"start": v(80.66, 76.07) * mm, "mid": v(78.8, 76.22) * mm, "end": v(77.2, 77.2) * mm});
            skArc(sketch, "E9.49.5", {"start": v(83.6, 76.97) * mm, "mid": v(82.16, 76.41) * mm, "end": v(80.66, 76.07) * mm});
            skLineSegment(sketch, "E9.49.6", {"start": v(83.6, 76.97) * mm, "end": v(84.66, 77.5) * mm});
            skArc(sketch, "E9.49.7", {"start": v(84.66, 77.5) * mm, "mid": v(86, 77.97) * mm, "end": v(87.43, 78.13) * mm});
            skArc(sketch, "E9.50.0", {"start": v(67.52, 92.8) * mm, "mid": v(67.85, 94.2) * mm, "end": v(67.85, 95.63) * mm});
            skLineSegment(sketch, "E9.50.1", {"start": v(67.13, 91.69) * mm, "end": v(67.52, 92.8) * mm});
            skArc(sketch, "E9.50.2", {"start": v(67.13, 91.69) * mm, "mid": v(66.73, 90.2) * mm, "end": v(66.56, 88.67) * mm});
            skArc(sketch, "E9.50.3", {"start": v(66.56, 88.67) * mm, "mid": v(66.92, 86.83) * mm, "end": v(68.07, 85.36) * mm});
            skArc(sketch, "E9.50.4", {"start": v(71.64, 84.62) * mm, "mid": v(69.77, 84.56) * mm, "end": v(68.07, 85.36) * mm});
            skArc(sketch, "E9.50.5", {"start": v(74.45, 85.85) * mm, "mid": v(73.09, 85.13) * mm, "end": v(71.64, 84.62) * mm});
            skLineSegment(sketch, "E9.50.6", {"start": v(74.45, 85.85) * mm, "end": v(75.45, 86.48) * mm});
            skArc(sketch, "E9.50.7", {"start": v(75.45, 86.48) * mm, "mid": v(76.74, 87.1) * mm, "end": v(78.13, 87.43) * mm});
            skArc(sketch, "E9.51.0", {"start": v(56.7, 99.78) * mm, "mid": v(56.88, 101.2) * mm, "end": v(56.72, 102.63) * mm});
            skLineSegment(sketch, "E9.51.1", {"start": v(56.44, 98.63) * mm, "end": v(56.7, 99.78) * mm});
            skArc(sketch, "E9.51.2", {"start": v(56.44, 98.63) * mm, "mid": v(56.22, 97.1) * mm, "end": v(56.22, 95.57) * mm});
            skArc(sketch, "E9.51.3", {"start": v(56.22, 95.57) * mm, "mid": v(56.78, 93.78) * mm, "end": v(58.09, 92.44) * mm});
            skArc(sketch, "E9.51.4", {"start": v(61.71, 92.11) * mm, "mid": v(59.86, 91.84) * mm, "end": v(58.09, 92.44) * mm});
            skArc(sketch, "E9.51.5", {"start": v(64.37, 93.65) * mm, "mid": v(63.1, 92.78) * mm, "end": v(61.71, 92.11) * mm});
            skLineSegment(sketch, "E9.51.6", {"start": v(64.37, 93.65) * mm, "end": v(65.3, 94.39) * mm});
            skArc(sketch, "E9.51.7", {"start": v(65.3, 94.39) * mm, "mid": v(66.5, 95.15) * mm, "end": v(67.85, 95.63) * mm});
            skArc(sketch, "E9.52.0", {"start": v(45.18, 105.5) * mm, "mid": v(45.19, 106.93) * mm, "end": v(44.87, 108.33) * mm});
            skLineSegment(sketch, "E9.52.1", {"start": v(45.04, 104.33) * mm, "end": v(45.18, 105.5) * mm});
            skArc(sketch, "E9.52.2", {"start": v(45.04, 104.33) * mm, "mid": v(44.99, 102.79) * mm, "end": v(45.16, 101.26) * mm});
            skArc(sketch, "E9.52.3", {"start": v(45.16, 101.26) * mm, "mid": v(45.92, 99.55) * mm, "end": v(47.37, 98.36) * mm});
            skArc(sketch, "E9.52.4", {"start": v(51, 98.44) * mm, "mid": v(49.2, 97.97) * mm, "end": v(47.37, 98.36) * mm});
            skArc(sketch, "E9.52.5", {"start": v(53.48, 100.26) * mm, "mid": v(52.31, 99.26) * mm, "end": v(51, 98.44) * mm});
            skLineSegment(sketch, "E9.52.6", {"start": v(53.48, 100.26) * mm, "end": v(54.31, 101.1) * mm});
            skArc(sketch, "E9.52.7", {"start": v(54.31, 101.1) * mm, "mid": v(55.43, 102) * mm, "end": v(56.72, 102.63) * mm});
            skArc(sketch, "E9.53.0", {"start": v(33.09, 109.9) * mm, "mid": v(32.93, 111.32) * mm, "end": v(32.46, 112.68) * mm});
            skLineSegment(sketch, "E9.53.1", {"start": v(33.08, 108.71) * mm, "end": v(33.09, 109.9) * mm});
            skArc(sketch, "E9.53.2", {"start": v(33.08, 108.71) * mm, "mid": v(33.2, 107.18) * mm, "end": v(33.54, 105.68) * mm});
            skArc(sketch, "E9.53.3", {"start": v(33.54, 105.68) * mm, "mid": v(34.48, 104.06) * mm, "end": v(36.06, 103.05) * mm});
            skArc(sketch, "E9.53.4", {"start": v(39.67, 103.54) * mm, "mid": v(37.92, 102.86) * mm, "end": v(36.06, 103.05) * mm});
            skArc(sketch, "E9.53.5", {"start": v(41.92, 105.62) * mm, "mid": v(40.87, 104.5) * mm, "end": v(39.67, 103.54) * mm});
            skLineSegment(sketch, "E9.53.6", {"start": v(41.92, 105.62) * mm, "end": v(42.65, 106.55) * mm});
            skArc(sketch, "E9.53.7", {"start": v(42.65, 106.55) * mm, "mid": v(43.66, 107.57) * mm, "end": v(44.87, 108.33) * mm});
            skArc(sketch, "E9.54.0", {"start": v(20.57, 112.9) * mm, "mid": v(20.26, 114.3) * mm, "end": v(19.64, 115.6) * mm});
            skLineSegment(sketch, "E9.54.1", {"start": v(20.7, 111.74) * mm, "end": v(20.57, 112.9) * mm});
            skArc(sketch, "E9.54.2", {"start": v(20.7, 111.74) * mm, "mid": v(20.99, 110.22) * mm, "end": v(21.5, 108.77) * mm});
            skArc(sketch, "E9.54.3", {"start": v(21.5, 108.77) * mm, "mid": v(22.62, 107.27) * mm, "end": v(24.3, 106.44) * mm});
            skArc(sketch, "E9.54.4", {"start": v(27.83, 107.33) * mm, "mid": v(26.17, 106.46) * mm, "end": v(24.3, 106.44) * mm});
            skArc(sketch, "E9.54.5", {"start": v(29.83, 109.65) * mm, "mid": v(28.91, 108.41) * mm, "end": v(27.83, 107.33) * mm});
            skLineSegment(sketch, "E9.54.6", {"start": v(29.83, 109.65) * mm, "end": v(30.45, 110.65) * mm});
            skArc(sketch, "E9.54.7", {"start": v(30.45, 110.65) * mm, "mid": v(31.34, 111.78) * mm, "end": v(32.46, 112.68) * mm});
            skArc(sketch, "E9.55.0", {"start": v(7.8, 114.5) * mm, "mid": v(7.33, 115.86) * mm, "end": v(6.57, 117.07) * mm});
            skLineSegment(sketch, "E9.55.1", {"start": v(8.06, 113.35) * mm, "end": v(7.8, 114.5) * mm});
            skArc(sketch, "E9.55.2", {"start": v(8.06, 113.35) * mm, "mid": v(8.52, 111.88) * mm, "end": v(9.18, 110.5) * mm});
            skArc(sketch, "E9.55.3", {"start": v(9.18, 110.5) * mm, "mid": v(10.46, 109.13) * mm, "end": v(12.22, 108.49) * mm});
            skArc(sketch, "E9.55.4", {"start": v(15.63, 109.77) * mm, "mid": v(14.08, 108.72) * mm, "end": v(12.22, 108.49) * mm});
            skArc(sketch, "E9.55.5", {"start": v(17.36, 112.3) * mm, "mid": v(16.6, 110.97) * mm, "end": v(15.63, 109.77) * mm});
            skLineSegment(sketch, "E9.55.6", {"start": v(17.36, 112.3) * mm, "end": v(17.87, 113.37) * mm});
            skArc(sketch, "E9.55.7", {"start": v(17.87, 113.37) * mm, "mid": v(18.63, 114.58) * mm, "end": v(19.64, 115.6) * mm});
            skPoint(sketch, "E9.center", {"position": v(0, 0) * mm});
            skCircle(sketch, "E10", {"center": v(0, 0) * mm, "radius": 115.64 * mm});
            skCircle(sketch, "E11", {"center": v(0, 0) * mm, "radius": 65 * mm});
            skCircle(sketch, "E12", {"center": v(0, 72) * mm, "radius": 5.25 * mm});
            skCircle(sketch, "E13.1.0", {"center": v(-68.48, 22.25) * mm, "radius": 5.25 * mm});
            skCircle(sketch, "E13.2.0", {"center": v(-42.32, -58.25) * mm, "radius": 5.25 * mm});
            skCircle(sketch, "E13.3.0", {"center": v(42.32, -58.25) * mm, "radius": 5.25 * mm});
            skCircle(sketch, "E13.4.0", {"center": v(68.48, 22.25) * mm, "radius": 5.25 * mm});
            skCircle(sketch, "E14", {"center": v(0, 0) * mm, "radius": 106.68 * mm});
            skSolve(sketch);
        }
        {
            var Q0;
            Q0=makeQuery(id+"F0.imprint","IMPRINT",FACE,{"disambiguationData":[TD([[makeQuery(id+"F0.imprint","IMPRINT",EDGE,{"derivedFrom":sQuery(id+"F0.wireOp",EDGE,"E11")}),-1.0]])]});
            extrude(context, id + "F1", {"entities" : qUnion([Q0]), "endBound" : BoundingType.SYMMETRIC, "oppositeDirection" : true, "depth" : 4.5 * mm});
        }
        {
            var Q0;
            Q0=makeQuery(id+"F0.imprint","IMPRINT",FACE,{"disambiguationData":[TD([[makeQuery(id+"F0.imprint","IMPRINT",EDGE,{"derivedFrom":sQuery(id+"F0.wireOp",EDGE,"E0")}),-1.0]])]});
            extrude(context, id + "F2", {"entities" : qUnion([Q0]), "operationType" : NewBodyOperationType.ADD, "endBound" : BoundingType.SYMMETRIC, "depth" : 3.16 * mm});
        }
        {
            var Q0;
            Q0=makeQuery(id+"F1.opExtrude","CAP_FACE",FACE,{"disambiguationData":[OSD([sQuery(id+"F0.wireOp",EDGE,"E11"),sQuery(id+"F0.wireOp",EDGE,"E12"),sQuery(id+"F0.wireOp",EDGE,"E13.1.0"),sQuery(id+"F0.wireOp",EDGE,"E13.2.0"),sQuery(id+"F0.wireOp",EDGE,"E13.3.0"),sQuery(id+"F0.wireOp",EDGE,"E13.4.0"),sQuery(id+"F0.wireOp",EDGE,"E14")])],"isStart":true});
            var sketch = newSketch(context, id + "F3", { "sketchPlane" : qUnion([Q0])});
            skArc(sketch, "E15", {"start": v(70.9, -72.78) * mm, "mid": v(75.8, -67.65) * mm, "end": v(80.33, -62.2) * mm});
            skArc(sketch, "E16", {"start": v(48.9, -50.2) * mm, "mid": v(52.28, -46.66) * mm, "end": v(55.41, -42.9) * mm});
            skLineSegment(sketch, "E17", {"start": v(69.07, 11.87) * mm, "end": v(100.13, 17.2) * mm});
            skLineSegment(sketch, "E18", {"start": v(48.9, -50.2) * mm, "end": v(70.9, -72.78) * mm});
            skLineSegment(sketch, "E19", {"start": v(70.05, 2.14) * mm, "end": v(101.55, 3.1) * mm});
            skLineSegment(sketch, "E20", {"start": v(70.08, 0.3) * mm, "end": v(101.6, 0.45) * mm});
            skLineSegment(sketch, "E21", {"start": v(69.44, -9.45) * mm, "end": v(100.67, -13.7) * mm});
            skLineSegment(sketch, "E22", {"start": v(69.17, -11.26) * mm, "end": v(100.28, -16.33) * mm});
            skLineSegment(sketch, "E23", {"start": v(66.93, -20.78) * mm, "end": v(97.03, -30.13) * mm});
            skLineSegment(sketch, "E24", {"start": v(66.36, -22.53) * mm, "end": v(96.2, -32.66) * mm});
            skLineSegment(sketch, "E25", {"start": v(62.58, -31.54) * mm, "end": v(90.72, -45.73) * mm});
            skLineSegment(sketch, "E26", {"start": v(61.73, -33.17) * mm, "end": v(89.5, -48.09) * mm});
            skLineSegment(sketch, "E27", {"start": v(56.52, -41.44) * mm, "end": v(81.93, -60.07) * mm});
            skLineSegment(sketch, "E28", {"start": v(55.41, -42.9) * mm, "end": v(80.33, -62.2) * mm});
            skArc(sketch, "E29.trimOffspring", {"start": v(56.52, -41.44) * mm, "mid": v(59.27, -37.4) * mm, "end": v(61.73, -33.17) * mm});
            skArc(sketch, "E30.trimOffspring", {"start": v(81.93, -60.07) * mm, "mid": v(85.92, -54.21) * mm, "end": v(89.5, -48.09) * mm});
            skArc(sketch, "E31.trimOffspring", {"start": v(90.72, -45.73) * mm, "mid": v(93.7, -39.29) * mm, "end": v(96.2, -32.66) * mm});
            skArc(sketch, "E32.trimOffspring", {"start": v(97.03, -30.13) * mm, "mid": v(98.9, -23.28) * mm, "end": v(100.28, -16.33) * mm});
            skArc(sketch, "E33.trimOffspring", {"start": v(100.67, -13.7) * mm, "mid": v(101.38, -6.64) * mm, "end": v(101.6, 0.45) * mm});
            skArc(sketch, "E34.trimOffspring", {"start": v(101.55, 3.1) * mm, "mid": v(101.09, 10.18) * mm, "end": v(100.13, 17.2) * mm});
            skArc(sketch, "E35.trimOffspring", {"start": v(70.05, 2.14) * mm, "mid": v(69.73, 7.02) * mm, "end": v(69.07, 11.87) * mm});
            skArc(sketch, "E36.trimOffspring", {"start": v(69.44, -9.45) * mm, "mid": v(69.93, -4.58) * mm, "end": v(70.08, 0.3) * mm});
            skArc(sketch, "E37.trimOffspring", {"start": v(66.93, -20.78) * mm, "mid": v(68.21, -16.06) * mm, "end": v(69.17, -11.26) * mm});
            skArc(sketch, "E38.trimOffspring", {"start": v(62.58, -31.54) * mm, "mid": v(64.63, -27.1) * mm, "end": v(66.36, -22.53) * mm});
            skLineSegment(sketch, "E39.1.0", {"start": v(10.05, 69.35) * mm, "end": v(14.58, 100.55) * mm});
            skLineSegment(sketch, "E39.1.1", {"start": v(19.6, 67.28) * mm, "end": v(28.43, 97.54) * mm});
            skLineSegment(sketch, "E39.1.2", {"start": v(21.36, 66.74) * mm, "end": v(30.97, 96.76) * mm});
            skLineSegment(sketch, "E39.1.3", {"start": v(30.44, 63.12) * mm, "end": v(44.14, 91.5) * mm});
            skLineSegment(sketch, "E39.1.4", {"start": v(32.09, 62.3) * mm, "end": v(46.52, 90.32) * mm});
            skArc(sketch, "E39.1.5", {"start": v(28.43, 97.54) * mm, "mid": v(21.55, 99.28) * mm, "end": v(14.58, 100.55) * mm});
            skArc(sketch, "E39.1.6", {"start": v(19.6, 67.28) * mm, "mid": v(14.87, 68.48) * mm, "end": v(10.05, 69.35) * mm});
            skArc(sketch, "E39.1.7", {"start": v(30.44, 63.12) * mm, "mid": v(25.97, 65.1) * mm, "end": v(21.36, 66.74) * mm});
            skArc(sketch, "E39.1.8", {"start": v(44.14, 91.5) * mm, "mid": v(37.65, 94.36) * mm, "end": v(30.97, 96.76) * mm});
            skArc(sketch, "E39.1.9", {"start": v(58.63, 82.97) * mm, "mid": v(52.7, 86.86) * mm, "end": v(46.52, 90.32) * mm});
            skArc(sketch, "E39.1.10", {"start": v(40.45, 57.23) * mm, "mid": v(36.35, 59.91) * mm, "end": v(32.09, 62.3) * mm});
            skArc(sketch, "E39.1.11", {"start": v(49.34, 49.77) * mm, "mid": v(45.74, 53.1) * mm, "end": v(41.93, 56.15) * mm});
            skArc(sketch, "E39.1.12", {"start": v(56.87, 40.95) * mm, "mid": v(53.88, 44.81) * mm, "end": v(50.62, 48.46) * mm});
            skArc(sketch, "E39.1.13", {"start": v(62.85, 31) * mm, "mid": v(60.54, 35.3) * mm, "end": v(57.93, 39.44) * mm});
            skLineSegment(sketch, "E39.1.14", {"start": v(40.45, 57.23) * mm, "end": v(58.63, 82.97) * mm});
            skLineSegment(sketch, "E39.1.15", {"start": v(41.93, 56.15) * mm, "end": v(60.79, 81.4) * mm});
            skLineSegment(sketch, "E39.1.16", {"start": v(49.34, 49.77) * mm, "end": v(71.52, 72.15) * mm});
            skLineSegment(sketch, "E39.1.17", {"start": v(50.62, 48.46) * mm, "end": v(73.39, 70.26) * mm});
            skArc(sketch, "E39.1.18", {"start": v(71.52, 72.15) * mm, "mid": v(66.32, 76.97) * mm, "end": v(60.79, 81.4) * mm});
            skArc(sketch, "E39.1.19", {"start": v(82.45, 59.36) * mm, "mid": v(78.11, 64.97) * mm, "end": v(73.39, 70.26) * mm});
            skLineSegment(sketch, "E39.1.20", {"start": v(56.87, 40.95) * mm, "end": v(82.45, 59.36) * mm});
            skLineSegment(sketch, "E39.1.21", {"start": v(57.93, 39.44) * mm, "end": v(83.98, 57.18) * mm});
            skArc(sketch, "E39.1.22", {"start": v(91.12, 44.93) * mm, "mid": v(87.76, 51.18) * mm, "end": v(83.98, 57.18) * mm});
            skLineSegment(sketch, "E39.1.23", {"start": v(62.85, 31) * mm, "end": v(91.12, 44.93) * mm});
            skLineSegment(sketch, "E39.2.0", {"start": v(-62.85, 31) * mm, "end": v(-91.12, 44.93) * mm});
            skLineSegment(sketch, "E39.2.1", {"start": v(-57.93, 39.44) * mm, "end": v(-83.98, 57.18) * mm});
            skLineSegment(sketch, "E39.2.2", {"start": v(-56.88, 40.94) * mm, "end": v(-82.45, 59.36) * mm});
            skLineSegment(sketch, "E39.2.3", {"start": v(-50.62, 48.46) * mm, "end": v(-73.4, 70.25) * mm});
            skLineSegment(sketch, "E39.2.4", {"start": v(-49.34, 49.77) * mm, "end": v(-71.53, 72.15) * mm});
            skArc(sketch, "E39.2.5", {"start": v(-83.98, 57.18) * mm, "mid": v(-87.76, 51.18) * mm, "end": v(-91.12, 44.93) * mm});
            skArc(sketch, "E39.2.6", {"start": v(-57.93, 39.44) * mm, "mid": v(-60.54, 35.3) * mm, "end": v(-62.85, 31) * mm});
            skArc(sketch, "E39.2.7", {"start": v(-50.62, 48.46) * mm, "mid": v(-53.88, 44.81) * mm, "end": v(-56.88, 40.94) * mm});
            skArc(sketch, "E39.2.8", {"start": v(-73.4, 70.25) * mm, "mid": v(-78.11, 64.96) * mm, "end": v(-82.45, 59.36) * mm});
            skArc(sketch, "E39.2.9", {"start": v(-60.79, 81.4) * mm, "mid": v(-66.32, 76.96) * mm, "end": v(-71.53, 72.15) * mm});
            skArc(sketch, "E39.2.10", {"start": v(-41.93, 56.15) * mm, "mid": v(-45.75, 53.09) * mm, "end": v(-49.34, 49.77) * mm});
            skArc(sketch, "E39.2.11", {"start": v(-32.09, 62.3) * mm, "mid": v(-36.36, 59.91) * mm, "end": v(-40.45, 57.23) * mm});
            skArc(sketch, "E39.2.12", {"start": v(-21.37, 66.74) * mm, "mid": v(-25.97, 65.1) * mm, "end": v(-30.45, 63.12) * mm});
            skArc(sketch, "E39.2.13", {"start": v(-10.05, 69.35) * mm, "mid": v(-14.87, 68.48) * mm, "end": v(-19.61, 67.28) * mm});
            skLineSegment(sketch, "E39.2.14", {"start": v(-41.93, 56.15) * mm, "end": v(-60.79, 81.4) * mm});
            skLineSegment(sketch, "E39.2.15", {"start": v(-40.45, 57.23) * mm, "end": v(-58.64, 82.97) * mm});
            skLineSegment(sketch, "E39.2.16", {"start": v(-32.09, 62.3) * mm, "end": v(-46.52, 90.32) * mm});
            skLineSegment(sketch, "E39.2.17", {"start": v(-30.45, 63.12) * mm, "end": v(-44.14, 91.5) * mm});
            skArc(sketch, "E39.2.18", {"start": v(-46.52, 90.32) * mm, "mid": v(-52.7, 86.85) * mm, "end": v(-58.64, 82.97) * mm});
            skArc(sketch, "E39.2.19", {"start": v(-30.98, 96.76) * mm, "mid": v(-37.65, 94.36) * mm, "end": v(-44.14, 91.5) * mm});
            skLineSegment(sketch, "E39.2.20", {"start": v(-21.37, 66.74) * mm, "end": v(-30.98, 96.76) * mm});
            skLineSegment(sketch, "E39.2.21", {"start": v(-19.61, 67.28) * mm, "end": v(-28.43, 97.54) * mm});
            skArc(sketch, "E39.2.22", {"start": v(-14.58, 100.55) * mm, "mid": v(-21.56, 99.28) * mm, "end": v(-28.43, 97.54) * mm});
            skLineSegment(sketch, "E39.2.23", {"start": v(-10.05, 69.35) * mm, "end": v(-14.58, 100.55) * mm});
            skLineSegment(sketch, "E39.3.0", {"start": v(-48.9, -50.2) * mm, "end": v(-70.9, -72.78) * mm});
            skLineSegment(sketch, "E39.3.1", {"start": v(-55.41, -42.9) * mm, "end": v(-80.33, -62.2) * mm});
            skLineSegment(sketch, "E39.3.2", {"start": v(-56.51, -41.44) * mm, "end": v(-81.93, -60.08) * mm});
            skLineSegment(sketch, "E39.3.3", {"start": v(-61.73, -33.17) * mm, "end": v(-89.5, -48.09) * mm});
            skLineSegment(sketch, "E39.3.4", {"start": v(-62.58, -31.54) * mm, "end": v(-90.72, -45.73) * mm});
            skArc(sketch, "E39.3.5", {"start": v(-80.33, -62.2) * mm, "mid": v(-75.8, -67.65) * mm, "end": v(-70.9, -72.78) * mm});
            skArc(sketch, "E39.3.6", {"start": v(-55.41, -42.9) * mm, "mid": v(-52.28, -46.67) * mm, "end": v(-48.9, -50.2) * mm});
            skArc(sketch, "E39.3.7", {"start": v(-61.73, -33.17) * mm, "mid": v(-59.27, -37.4) * mm, "end": v(-56.51, -41.44) * mm});
            skArc(sketch, "E39.3.8", {"start": v(-89.5, -48.09) * mm, "mid": v(-85.92, -54.22) * mm, "end": v(-81.93, -60.08) * mm});
            skArc(sketch, "E39.3.9", {"start": v(-96.2, -32.66) * mm, "mid": v(-93.7, -39.3) * mm, "end": v(-90.72, -45.73) * mm});
            skArc(sketch, "E39.3.10", {"start": v(-66.36, -22.53) * mm, "mid": v(-64.63, -27.1) * mm, "end": v(-62.58, -31.54) * mm});
            skArc(sketch, "E39.3.11", {"start": v(-69.17, -11.27) * mm, "mid": v(-68.21, -16.06) * mm, "end": v(-66.93, -20.78) * mm});
            skArc(sketch, "E39.3.12", {"start": v(-70.08, 0.3) * mm, "mid": v(-69.93, -4.58) * mm, "end": v(-69.44, -9.45) * mm});
            skArc(sketch, "E39.3.13", {"start": v(-69.07, 11.87) * mm, "mid": v(-69.73, 7.02) * mm, "end": v(-70.05, 2.14) * mm});
            skLineSegment(sketch, "E39.3.14", {"start": v(-66.36, -22.53) * mm, "end": v(-96.2, -32.66) * mm});
            skLineSegment(sketch, "E39.3.15", {"start": v(-66.93, -20.78) * mm, "end": v(-97.03, -30.13) * mm});
            skLineSegment(sketch, "E39.3.16", {"start": v(-69.17, -11.27) * mm, "end": v(-100.27, -16.33) * mm});
            skLineSegment(sketch, "E39.3.17", {"start": v(-69.44, -9.45) * mm, "end": v(-100.67, -13.7) * mm});
            skArc(sketch, "E39.3.18", {"start": v(-100.27, -16.33) * mm, "mid": v(-98.9, -23.29) * mm, "end": v(-97.03, -30.13) * mm});
            skArc(sketch, "E39.3.19", {"start": v(-101.6, 0.44) * mm, "mid": v(-101.38, -6.65) * mm, "end": v(-100.67, -13.7) * mm});
            skLineSegment(sketch, "E39.3.20", {"start": v(-70.08, 0.3) * mm, "end": v(-101.6, 0.44) * mm});
            skLineSegment(sketch, "E39.3.21", {"start": v(-70.05, 2.14) * mm, "end": v(-101.55, 3.1) * mm});
            skArc(sketch, "E39.3.22", {"start": v(-100.13, 17.2) * mm, "mid": v(-101.09, 10.18) * mm, "end": v(-101.55, 3.1) * mm});
            skLineSegment(sketch, "E39.3.23", {"start": v(-69.07, 11.87) * mm, "end": v(-100.13, 17.2) * mm});
            skSolve(sketch);
        }
        {
            var Q0;
            Q0=makeQuery(id+"F3.imprint","IMPRINT",FACE,{"disambiguationData":[TD([[makeQuery(id+"F3.imprint","IMPRINT",EDGE,{"derivedFrom":sQuery(id+"F3.wireOp",EDGE,"E17")}),-1.0]])]});
            var Q1;
            Q1=makeQuery(id+"F3.imprint","IMPRINT",FACE,{"disambiguationData":[TD([[makeQuery(id+"F3.imprint","IMPRINT",EDGE,{"derivedFrom":sQuery(id+"F3.wireOp",EDGE,"E20")}),-1.0]])]});
            var Q2;
            Q2=makeQuery(id+"F3.imprint","IMPRINT",FACE,{"disambiguationData":[TD([[makeQuery(id+"F3.imprint","IMPRINT",EDGE,{"derivedFrom":sQuery(id+"F3.wireOp",EDGE,"E22")}),-1.0]])]});
            var Q3;
            Q3=makeQuery(id+"F3.imprint","IMPRINT",FACE,{"disambiguationData":[TD([[makeQuery(id+"F3.imprint","IMPRINT",EDGE,{"derivedFrom":sQuery(id+"F3.wireOp",EDGE,"E39.3.0")}),-1.0]])]});
            var Q4;
            Q4=makeQuery(id+"F3.imprint","IMPRINT",FACE,{"disambiguationData":[TD([[makeQuery(id+"F3.imprint","IMPRINT",EDGE,{"derivedFrom":sQuery(id+"F3.wireOp",EDGE,"E39.3.2")}),-1.0]])]});
            var Q5;
            Q5=makeQuery(id+"F3.imprint","IMPRINT",FACE,{"disambiguationData":[TD([[makeQuery(id+"F3.imprint","IMPRINT",EDGE,{"derivedFrom":sQuery(id+"F3.wireOp",EDGE,"E39.3.4")}),-1.0]])]});
            var Q6;
            Q6=makeQuery(id+"F3.imprint","IMPRINT",FACE,{"disambiguationData":[TD([[makeQuery(id+"F3.imprint","IMPRINT",EDGE,{"derivedFrom":sQuery(id+"F3.wireOp",EDGE,"E39.2.0")}),-1.0]])]});
            var Q7;
            Q7=makeQuery(id+"F3.imprint","IMPRINT",FACE,{"disambiguationData":[TD([[makeQuery(id+"F3.imprint","IMPRINT",EDGE,{"derivedFrom":sQuery(id+"F3.wireOp",EDGE,"E39.2.2")}),-1.0]])]});
            var Q8;
            Q8=makeQuery(id+"F3.imprint","IMPRINT",FACE,{"disambiguationData":[TD([[makeQuery(id+"F3.imprint","IMPRINT",EDGE,{"derivedFrom":sQuery(id+"F3.wireOp",EDGE,"E39.2.4")}),-1.0]])]});
            var Q9;
            Q9=makeQuery(id+"F3.imprint","IMPRINT",FACE,{"disambiguationData":[TD([[makeQuery(id+"F3.imprint","IMPRINT",EDGE,{"derivedFrom":sQuery(id+"F3.wireOp",EDGE,"E39.1.0")}),-1.0]])]});
            var Q10;
            Q10=makeQuery(id+"F3.imprint","IMPRINT",FACE,{"disambiguationData":[TD([[makeQuery(id+"F3.imprint","IMPRINT",EDGE,{"derivedFrom":sQuery(id+"F3.wireOp",EDGE,"E39.1.2")}),-1.0]])]});
            var Q11;
            Q11=makeQuery(id+"F3.imprint","IMPRINT",FACE,{"disambiguationData":[TD([[makeQuery(id+"F3.imprint","IMPRINT",EDGE,{"derivedFrom":sQuery(id+"F3.wireOp",EDGE,"E39.1.4")}),-1.0]])]});
            extrude(context, id + "F4", {"entities" : qUnion([Q0, Q1, Q2, Q3, Q4, Q5, Q6, Q7, Q8, Q9, Q10, Q11]), "operationType" : NewBodyOperationType.REMOVE, "oppositeDirection" : true, "depth" : 4.5 * mm});
        }
        {
            var Q0;
            Q0=makeQuery(id+"F3.imprint","IMPRINT",FACE,{"disambiguationData":[TD([[makeQuery(id+"F3.imprint","IMPRINT",EDGE,{"derivedFrom":sQuery(id+"F3.wireOp",EDGE,"E24")}),-1.0]])]});
            var Q1;
            Q1=makeQuery(id+"F3.imprint","IMPRINT",FACE,{"disambiguationData":[TD([[makeQuery(id+"F3.imprint","IMPRINT",EDGE,{"derivedFrom":sQuery(id+"F3.wireOp",EDGE,"E26")}),-1.0]])]});
            var Q2;
            Q2=makeQuery(id+"F3.imprint","IMPRINT",FACE,{"disambiguationData":[TD([[makeQuery(id+"F3.imprint","IMPRINT",EDGE,{"derivedFrom":sQuery(id+"F3.wireOp",EDGE,"E15")}),1.0]])]});
            var Q3;
            Q3=makeQuery(id+"F3.imprint","IMPRINT",FACE,{"disambiguationData":[TD([[makeQuery(id+"F3.imprint","IMPRINT",EDGE,{"derivedFrom":sQuery(id+"F3.wireOp",EDGE,"E39.3.11")}),-1.0]])]});
            var Q4;
            Q4=makeQuery(id+"F3.imprint","IMPRINT",FACE,{"disambiguationData":[TD([[makeQuery(id+"F3.imprint","IMPRINT",EDGE,{"derivedFrom":sQuery(id+"F3.wireOp",EDGE,"E39.3.12")}),-1.0]])]});
            var Q5;
            Q5=makeQuery(id+"F3.imprint","IMPRINT",FACE,{"disambiguationData":[TD([[makeQuery(id+"F3.imprint","IMPRINT",EDGE,{"derivedFrom":sQuery(id+"F3.wireOp",EDGE,"E39.3.13")}),-1.0]])]});
            var Q6;
            Q6=makeQuery(id+"F3.imprint","IMPRINT",FACE,{"disambiguationData":[TD([[makeQuery(id+"F3.imprint","IMPRINT",EDGE,{"derivedFrom":sQuery(id+"F3.wireOp",EDGE,"E39.2.11")}),-1.0]])]});
            var Q7;
            Q7=makeQuery(id+"F3.imprint","IMPRINT",FACE,{"disambiguationData":[TD([[makeQuery(id+"F3.imprint","IMPRINT",EDGE,{"derivedFrom":sQuery(id+"F3.wireOp",EDGE,"E39.2.12")}),-1.0]])]});
            var Q8;
            Q8=makeQuery(id+"F3.imprint","IMPRINT",FACE,{"disambiguationData":[TD([[makeQuery(id+"F3.imprint","IMPRINT",EDGE,{"derivedFrom":sQuery(id+"F3.wireOp",EDGE,"E39.2.13")}),-1.0]])]});
            var Q9;
            Q9=makeQuery(id+"F3.imprint","IMPRINT",FACE,{"disambiguationData":[TD([[makeQuery(id+"F3.imprint","IMPRINT",EDGE,{"derivedFrom":sQuery(id+"F3.wireOp",EDGE,"E39.1.11")}),-1.0]])]});
            var Q10;
            Q10=makeQuery(id+"F3.imprint","IMPRINT",FACE,{"disambiguationData":[TD([[makeQuery(id+"F3.imprint","IMPRINT",EDGE,{"derivedFrom":sQuery(id+"F3.wireOp",EDGE,"E39.1.12")}),-1.0]])]});
            var Q11;
            Q11=makeQuery(id+"F3.imprint","IMPRINT",FACE,{"disambiguationData":[TD([[makeQuery(id+"F3.imprint","IMPRINT",EDGE,{"derivedFrom":sQuery(id+"F3.wireOp",EDGE,"E39.1.13")}),-1.0]])]});
            extrude(context, id + "F5", {"entities" : qUnion([Q0, Q1, Q2, Q3, Q4, Q5, Q6, Q7, Q8, Q9, Q10, Q11]), "operationType" : NewBodyOperationType.REMOVE, "oppositeDirection" : true, "depth" : 2 * mm});
        }
        {
            var Q0;
            Q0=makeQuery(id+"F5.boolean.opBoolean","COPY",EDGE,{"derivedFrom":makeQuery(id+"F5.opExtrude","SWEPT_EDGE",EDGE,{"disambiguationData":[OSD([sQuery(id+"F3.wireOp",EDGE,"E16"),sQuery(id+"F3.wireOp",EDGE,"E18")])]})});
            var Q1;
            Q1=makeQuery(id+"F5.boolean.opBoolean","COPY",EDGE,{"derivedFrom":makeQuery(id+"F5.opExtrude","SWEPT_EDGE",EDGE,{"disambiguationData":[OSD([sQuery(id+"F3.wireOp",EDGE,"E27"),sQuery(id+"F3.wireOp",EDGE,"E29.trimOffspring")])]})});
            var Q2;
            Q2=makeQuery(id+"F5.boolean.opBoolean","COPY",EDGE,{"derivedFrom":makeQuery(id+"F5.opExtrude","SWEPT_EDGE",EDGE,{"disambiguationData":[OSD([sQuery(id+"F3.wireOp",EDGE,"E25"),sQuery(id+"F3.wireOp",EDGE,"E38.trimOffspring")])]})});
            var Q3;
            Q3=makeQuery(id+"F4.boolean.opBoolean","COPY",EDGE,{"derivedFrom":makeQuery(id+"F4.opExtrude","SWEPT_EDGE",EDGE,{"disambiguationData":[OSD([sQuery(id+"F3.wireOp",EDGE,"E23"),sQuery(id+"F3.wireOp",EDGE,"E37.trimOffspring")])]})});
            var Q4;
            Q4=makeQuery(id+"F4.boolean.opBoolean","COPY",EDGE,{"derivedFrom":makeQuery(id+"F4.opExtrude","SWEPT_EDGE",EDGE,{"disambiguationData":[OSD([sQuery(id+"F3.wireOp",EDGE,"E21"),sQuery(id+"F3.wireOp",EDGE,"E36.trimOffspring")])]})});
            var Q5;
            Q5=makeQuery(id+"F4.boolean.opBoolean","COPY",EDGE,{"derivedFrom":makeQuery(id+"F4.opExtrude","SWEPT_EDGE",EDGE,{"disambiguationData":[OSD([sQuery(id+"F3.wireOp",EDGE,"E19"),sQuery(id+"F3.wireOp",EDGE,"E35.trimOffspring")])]})});
            var Q6;
            Q6=makeQuery(id+"F5.boolean.opBoolean","COPY",EDGE,{"derivedFrom":makeQuery(id+"F5.opExtrude","SWEPT_EDGE",EDGE,{"disambiguationData":[OSD([sQuery(id+"F3.wireOp",EDGE,"E16"),sQuery(id+"F3.wireOp",EDGE,"E28")])]})});
            var Q7;
            Q7=makeQuery(id+"F5.boolean.opBoolean","COPY",EDGE,{"derivedFrom":makeQuery(id+"F5.opExtrude","SWEPT_EDGE",EDGE,{"disambiguationData":[OSD([sQuery(id+"F3.wireOp",EDGE,"E26"),sQuery(id+"F3.wireOp",EDGE,"E29.trimOffspring")])]})});
            var Q8;
            Q8=makeQuery(id+"F5.boolean.opBoolean","COPY",EDGE,{"derivedFrom":makeQuery(id+"F5.opExtrude","SWEPT_EDGE",EDGE,{"disambiguationData":[OSD([sQuery(id+"F3.wireOp",EDGE,"E24"),sQuery(id+"F3.wireOp",EDGE,"E38.trimOffspring")])]})});
            var Q9;
            Q9=makeQuery(id+"F4.boolean.opBoolean","COPY",EDGE,{"derivedFrom":makeQuery(id+"F4.opExtrude","SWEPT_EDGE",EDGE,{"disambiguationData":[OSD([sQuery(id+"F3.wireOp",EDGE,"E22"),sQuery(id+"F3.wireOp",EDGE,"E37.trimOffspring")])]})});
            var Q10;
            Q10=makeQuery(id+"F4.boolean.opBoolean","COPY",EDGE,{"derivedFrom":makeQuery(id+"F4.opExtrude","SWEPT_EDGE",EDGE,{"disambiguationData":[OSD([sQuery(id+"F3.wireOp",EDGE,"E20"),sQuery(id+"F3.wireOp",EDGE,"E36.trimOffspring")])]})});
            var Q11;
            Q11=makeQuery(id+"F4.boolean.opBoolean","COPY",EDGE,{"derivedFrom":makeQuery(id+"F4.opExtrude","SWEPT_EDGE",EDGE,{"disambiguationData":[OSD([sQuery(id+"F3.wireOp",EDGE,"E17"),sQuery(id+"F3.wireOp",EDGE,"E35.trimOffspring")])]})});
            var Q12;
            Q12=makeQuery(id+"F4.boolean.opBoolean","COPY",EDGE,{"derivedFrom":makeQuery(id+"F4.opExtrude","SWEPT_EDGE",EDGE,{"disambiguationData":[OSD([sQuery(id+"F3.wireOp",EDGE,"E19"),sQuery(id+"F3.wireOp",EDGE,"E34.trimOffspring")])]})});
            var Q13;
            Q13=makeQuery(id+"F4.boolean.opBoolean","COPY",EDGE,{"derivedFrom":makeQuery(id+"F4.opExtrude","SWEPT_EDGE",EDGE,{"disambiguationData":[OSD([sQuery(id+"F3.wireOp",EDGE,"E21"),sQuery(id+"F3.wireOp",EDGE,"E33.trimOffspring")])]})});
            var Q14;
            Q14=makeQuery(id+"F4.boolean.opBoolean","COPY",EDGE,{"derivedFrom":makeQuery(id+"F4.opExtrude","SWEPT_EDGE",EDGE,{"disambiguationData":[OSD([sQuery(id+"F3.wireOp",EDGE,"E23"),sQuery(id+"F3.wireOp",EDGE,"E32.trimOffspring")])]})});
            var Q15;
            Q15=makeQuery(id+"F5.boolean.opBoolean","COPY",EDGE,{"derivedFrom":makeQuery(id+"F5.opExtrude","SWEPT_EDGE",EDGE,{"disambiguationData":[OSD([sQuery(id+"F3.wireOp",EDGE,"E25"),sQuery(id+"F3.wireOp",EDGE,"E31.trimOffspring")])]})});
            var Q16;
            Q16=makeQuery(id+"F5.boolean.opBoolean","COPY",EDGE,{"derivedFrom":makeQuery(id+"F5.opExtrude","SWEPT_EDGE",EDGE,{"disambiguationData":[OSD([sQuery(id+"F3.wireOp",EDGE,"E27"),sQuery(id+"F3.wireOp",EDGE,"E30.trimOffspring")])]})});
            var Q17;
            Q17=makeQuery(id+"F5.boolean.opBoolean","COPY",EDGE,{"derivedFrom":makeQuery(id+"F5.opExtrude","SWEPT_EDGE",EDGE,{"disambiguationData":[OSD([sQuery(id+"F3.wireOp",EDGE,"E15"),sQuery(id+"F3.wireOp",EDGE,"E18")])]})});
            var Q18;
            Q18=makeQuery(id+"F5.boolean.opBoolean","COPY",EDGE,{"derivedFrom":makeQuery(id+"F5.opExtrude","SWEPT_EDGE",EDGE,{"disambiguationData":[OSD([sQuery(id+"F3.wireOp",EDGE,"E15"),sQuery(id+"F3.wireOp",EDGE,"E28")])]})});
            var Q19;
            Q19=makeQuery(id+"F5.boolean.opBoolean","COPY",EDGE,{"derivedFrom":makeQuery(id+"F5.opExtrude","SWEPT_EDGE",EDGE,{"disambiguationData":[OSD([sQuery(id+"F3.wireOp",EDGE,"E26"),sQuery(id+"F3.wireOp",EDGE,"E30.trimOffspring")])]})});
            var Q20;
            Q20=makeQuery(id+"F5.boolean.opBoolean","COPY",EDGE,{"derivedFrom":makeQuery(id+"F5.opExtrude","SWEPT_EDGE",EDGE,{"disambiguationData":[OSD([sQuery(id+"F3.wireOp",EDGE,"E24"),sQuery(id+"F3.wireOp",EDGE,"E31.trimOffspring")])]})});
            var Q21;
            Q21=makeQuery(id+"F4.boolean.opBoolean","COPY",EDGE,{"derivedFrom":makeQuery(id+"F4.opExtrude","SWEPT_EDGE",EDGE,{"disambiguationData":[OSD([sQuery(id+"F3.wireOp",EDGE,"E22"),sQuery(id+"F3.wireOp",EDGE,"E32.trimOffspring")])]})});
            var Q22;
            Q22=makeQuery(id+"F4.boolean.opBoolean","COPY",EDGE,{"derivedFrom":makeQuery(id+"F4.opExtrude","SWEPT_EDGE",EDGE,{"disambiguationData":[OSD([sQuery(id+"F3.wireOp",EDGE,"E20"),sQuery(id+"F3.wireOp",EDGE,"E33.trimOffspring")])]})});
            var Q23;
            Q23=makeQuery(id+"F4.boolean.opBoolean","COPY",EDGE,{"derivedFrom":makeQuery(id+"F4.opExtrude","SWEPT_EDGE",EDGE,{"disambiguationData":[OSD([sQuery(id+"F3.wireOp",EDGE,"E17"),sQuery(id+"F3.wireOp",EDGE,"E34.trimOffspring")])]})});
            var Q24;
            Q24=makeQuery(id+"F4.boolean.opBoolean","COPY",EDGE,{"derivedFrom":makeQuery(id+"F4.opExtrude","SWEPT_EDGE",EDGE,{"disambiguationData":[OSD([sQuery(id+"F3.wireOp",EDGE,"E39.3.0"),sQuery(id+"F3.wireOp",EDGE,"E39.3.5")])]})});
            var Q25;
            Q25=makeQuery(id+"F4.boolean.opBoolean","COPY",EDGE,{"derivedFrom":makeQuery(id+"F4.opExtrude","SWEPT_EDGE",EDGE,{"disambiguationData":[OSD([sQuery(id+"F3.wireOp",EDGE,"E39.3.2"),sQuery(id+"F3.wireOp",EDGE,"E39.3.8")])]})});
            var Q26;
            Q26=makeQuery(id+"F4.boolean.opBoolean","COPY",EDGE,{"derivedFrom":makeQuery(id+"F4.opExtrude","SWEPT_EDGE",EDGE,{"disambiguationData":[OSD([sQuery(id+"F3.wireOp",EDGE,"E39.3.4"),sQuery(id+"F3.wireOp",EDGE,"E39.3.9")])]})});
            var Q27;
            Q27=makeQuery(id+"F5.boolean.opBoolean","COPY",EDGE,{"derivedFrom":makeQuery(id+"F5.opExtrude","SWEPT_EDGE",EDGE,{"disambiguationData":[OSD([sQuery(id+"F3.wireOp",EDGE,"E39.3.15"),sQuery(id+"F3.wireOp",EDGE,"E39.3.18")])]})});
            var Q28;
            Q28=makeQuery(id+"F5.boolean.opBoolean","COPY",EDGE,{"derivedFrom":makeQuery(id+"F5.opExtrude","SWEPT_EDGE",EDGE,{"disambiguationData":[OSD([sQuery(id+"F3.wireOp",EDGE,"E39.3.17"),sQuery(id+"F3.wireOp",EDGE,"E39.3.19")])]})});
            var Q29;
            Q29=makeQuery(id+"F5.boolean.opBoolean","COPY",EDGE,{"derivedFrom":makeQuery(id+"F5.opExtrude","SWEPT_EDGE",EDGE,{"disambiguationData":[OSD([sQuery(id+"F3.wireOp",EDGE,"E39.3.21"),sQuery(id+"F3.wireOp",EDGE,"E39.3.22")])]})});
            var Q30;
            Q30=makeQuery(id+"F4.boolean.opBoolean","COPY",EDGE,{"derivedFrom":makeQuery(id+"F4.opExtrude","SWEPT_EDGE",EDGE,{"disambiguationData":[OSD([sQuery(id+"F3.wireOp",EDGE,"E39.3.1"),sQuery(id+"F3.wireOp",EDGE,"E39.3.5")])]})});
            var Q31;
            Q31=makeQuery(id+"F4.boolean.opBoolean","COPY",EDGE,{"derivedFrom":makeQuery(id+"F4.opExtrude","SWEPT_EDGE",EDGE,{"disambiguationData":[OSD([sQuery(id+"F3.wireOp",EDGE,"E39.3.3"),sQuery(id+"F3.wireOp",EDGE,"E39.3.8")])]})});
            var Q32;
            Q32=makeQuery(id+"F4.boolean.opBoolean","COPY",EDGE,{"derivedFrom":makeQuery(id+"F4.opExtrude","SWEPT_EDGE",EDGE,{"disambiguationData":[OSD([sQuery(id+"F3.wireOp",EDGE,"E39.3.9"),sQuery(id+"F3.wireOp",EDGE,"E39.3.14")])]})});
            var Q33;
            Q33=makeQuery(id+"F5.boolean.opBoolean","COPY",EDGE,{"derivedFrom":makeQuery(id+"F5.opExtrude","SWEPT_EDGE",EDGE,{"disambiguationData":[OSD([sQuery(id+"F3.wireOp",EDGE,"E39.3.16"),sQuery(id+"F3.wireOp",EDGE,"E39.3.18")])]})});
            var Q34;
            Q34=makeQuery(id+"F5.boolean.opBoolean","COPY",EDGE,{"derivedFrom":makeQuery(id+"F5.opExtrude","SWEPT_EDGE",EDGE,{"disambiguationData":[OSD([sQuery(id+"F3.wireOp",EDGE,"E39.3.19"),sQuery(id+"F3.wireOp",EDGE,"E39.3.20")])]})});
            var Q35;
            Q35=makeQuery(id+"F5.boolean.opBoolean","COPY",EDGE,{"derivedFrom":makeQuery(id+"F5.opExtrude","SWEPT_EDGE",EDGE,{"disambiguationData":[OSD([sQuery(id+"F3.wireOp",EDGE,"E39.3.22"),sQuery(id+"F3.wireOp",EDGE,"E39.3.23")])]})});
            var Q36;
            Q36=makeQuery(id+"F4.boolean.opBoolean","COPY",EDGE,{"derivedFrom":makeQuery(id+"F4.opExtrude","SWEPT_EDGE",EDGE,{"disambiguationData":[OSD([sQuery(id+"F3.wireOp",EDGE,"E39.3.1"),sQuery(id+"F3.wireOp",EDGE,"E39.3.6")])]})});
            var Q37;
            Q37=makeQuery(id+"F4.boolean.opBoolean","COPY",EDGE,{"derivedFrom":makeQuery(id+"F4.opExtrude","SWEPT_EDGE",EDGE,{"disambiguationData":[OSD([sQuery(id+"F3.wireOp",EDGE,"E39.3.3"),sQuery(id+"F3.wireOp",EDGE,"E39.3.7")])]})});
            var Q38;
            Q38=makeQuery(id+"F4.boolean.opBoolean","COPY",EDGE,{"derivedFrom":makeQuery(id+"F4.opExtrude","SWEPT_EDGE",EDGE,{"disambiguationData":[OSD([sQuery(id+"F3.wireOp",EDGE,"E39.3.10"),sQuery(id+"F3.wireOp",EDGE,"E39.3.14")])]})});
            var Q39;
            Q39=makeQuery(id+"F5.boolean.opBoolean","COPY",EDGE,{"derivedFrom":makeQuery(id+"F5.opExtrude","SWEPT_EDGE",EDGE,{"disambiguationData":[OSD([sQuery(id+"F3.wireOp",EDGE,"E39.3.11"),sQuery(id+"F3.wireOp",EDGE,"E39.3.16")])]})});
            var Q40;
            Q40=makeQuery(id+"F5.boolean.opBoolean","COPY",EDGE,{"derivedFrom":makeQuery(id+"F5.opExtrude","SWEPT_EDGE",EDGE,{"disambiguationData":[OSD([sQuery(id+"F3.wireOp",EDGE,"E39.3.12"),sQuery(id+"F3.wireOp",EDGE,"E39.3.20")])]})});
            var Q41;
            Q41=makeQuery(id+"F5.boolean.opBoolean","COPY",EDGE,{"derivedFrom":makeQuery(id+"F5.opExtrude","SWEPT_EDGE",EDGE,{"disambiguationData":[OSD([sQuery(id+"F3.wireOp",EDGE,"E39.3.13"),sQuery(id+"F3.wireOp",EDGE,"E39.3.23")])]})});
            var Q42;
            Q42=makeQuery(id+"F5.boolean.opBoolean","COPY",EDGE,{"derivedFrom":makeQuery(id+"F5.opExtrude","SWEPT_EDGE",EDGE,{"disambiguationData":[OSD([sQuery(id+"F3.wireOp",EDGE,"E39.3.13"),sQuery(id+"F3.wireOp",EDGE,"E39.3.21")])]})});
            var Q43;
            Q43=makeQuery(id+"F5.boolean.opBoolean","COPY",EDGE,{"derivedFrom":makeQuery(id+"F5.opExtrude","SWEPT_EDGE",EDGE,{"disambiguationData":[OSD([sQuery(id+"F3.wireOp",EDGE,"E39.3.12"),sQuery(id+"F3.wireOp",EDGE,"E39.3.17")])]})});
            var Q44;
            Q44=makeQuery(id+"F5.boolean.opBoolean","COPY",EDGE,{"derivedFrom":makeQuery(id+"F5.opExtrude","SWEPT_EDGE",EDGE,{"disambiguationData":[OSD([sQuery(id+"F3.wireOp",EDGE,"E39.3.11"),sQuery(id+"F3.wireOp",EDGE,"E39.3.15")])]})});
            var Q45;
            Q45=makeQuery(id+"F4.boolean.opBoolean","COPY",EDGE,{"derivedFrom":makeQuery(id+"F4.opExtrude","SWEPT_EDGE",EDGE,{"disambiguationData":[OSD([sQuery(id+"F3.wireOp",EDGE,"E39.3.4"),sQuery(id+"F3.wireOp",EDGE,"E39.3.10")])]})});
            var Q46;
            Q46=makeQuery(id+"F4.boolean.opBoolean","COPY",EDGE,{"derivedFrom":makeQuery(id+"F4.opExtrude","SWEPT_EDGE",EDGE,{"disambiguationData":[OSD([sQuery(id+"F3.wireOp",EDGE,"E39.3.2"),sQuery(id+"F3.wireOp",EDGE,"E39.3.7")])]})});
            var Q47;
            Q47=makeQuery(id+"F4.boolean.opBoolean","COPY",EDGE,{"derivedFrom":makeQuery(id+"F4.opExtrude","SWEPT_EDGE",EDGE,{"disambiguationData":[OSD([sQuery(id+"F3.wireOp",EDGE,"E39.3.0"),sQuery(id+"F3.wireOp",EDGE,"E39.3.6")])]})});
            var Q48;
            Q48=makeQuery(id+"F5.boolean.opBoolean","COPY",EDGE,{"derivedFrom":makeQuery(id+"F5.opExtrude","SWEPT_EDGE",EDGE,{"disambiguationData":[OSD([sQuery(id+"F3.wireOp",EDGE,"E39.2.13"),sQuery(id+"F3.wireOp",EDGE,"E39.2.21")])]})});
            var Q49;
            Q49=makeQuery(id+"F5.boolean.opBoolean","COPY",EDGE,{"derivedFrom":makeQuery(id+"F5.opExtrude","SWEPT_EDGE",EDGE,{"disambiguationData":[OSD([sQuery(id+"F3.wireOp",EDGE,"E39.2.12"),sQuery(id+"F3.wireOp",EDGE,"E39.2.17")])]})});
            var Q50;
            Q50=makeQuery(id+"F5.boolean.opBoolean","COPY",EDGE,{"derivedFrom":makeQuery(id+"F5.opExtrude","SWEPT_EDGE",EDGE,{"disambiguationData":[OSD([sQuery(id+"F3.wireOp",EDGE,"E39.2.11"),sQuery(id+"F3.wireOp",EDGE,"E39.2.15")])]})});
            var Q51;
            Q51=makeQuery(id+"F4.boolean.opBoolean","COPY",EDGE,{"derivedFrom":makeQuery(id+"F4.opExtrude","SWEPT_EDGE",EDGE,{"disambiguationData":[OSD([sQuery(id+"F3.wireOp",EDGE,"E39.2.4"),sQuery(id+"F3.wireOp",EDGE,"E39.2.10")])]})});
            var Q52;
            Q52=makeQuery(id+"F4.boolean.opBoolean","COPY",EDGE,{"derivedFrom":makeQuery(id+"F4.opExtrude","SWEPT_EDGE",EDGE,{"disambiguationData":[OSD([sQuery(id+"F3.wireOp",EDGE,"E39.2.2"),sQuery(id+"F3.wireOp",EDGE,"E39.2.7")])]})});
            var Q53;
            Q53=makeQuery(id+"F4.boolean.opBoolean","COPY",EDGE,{"derivedFrom":makeQuery(id+"F4.opExtrude","SWEPT_EDGE",EDGE,{"disambiguationData":[OSD([sQuery(id+"F3.wireOp",EDGE,"E39.2.0"),sQuery(id+"F3.wireOp",EDGE,"E39.2.6")])]})});
            var Q54;
            Q54=makeQuery(id+"F5.boolean.opBoolean","COPY",EDGE,{"derivedFrom":makeQuery(id+"F5.opExtrude","SWEPT_EDGE",EDGE,{"disambiguationData":[OSD([sQuery(id+"F3.wireOp",EDGE,"E39.2.13"),sQuery(id+"F3.wireOp",EDGE,"E39.2.23")])]})});
            var Q55;
            Q55=makeQuery(id+"F5.boolean.opBoolean","COPY",EDGE,{"derivedFrom":makeQuery(id+"F5.opExtrude","SWEPT_EDGE",EDGE,{"disambiguationData":[OSD([sQuery(id+"F3.wireOp",EDGE,"E39.2.12"),sQuery(id+"F3.wireOp",EDGE,"E39.2.20")])]})});
            var Q56;
            Q56=makeQuery(id+"F5.boolean.opBoolean","COPY",EDGE,{"derivedFrom":makeQuery(id+"F5.opExtrude","SWEPT_EDGE",EDGE,{"disambiguationData":[OSD([sQuery(id+"F3.wireOp",EDGE,"E39.2.11"),sQuery(id+"F3.wireOp",EDGE,"E39.2.16")])]})});
            var Q57;
            Q57=makeQuery(id+"F4.boolean.opBoolean","COPY",EDGE,{"derivedFrom":makeQuery(id+"F4.opExtrude","SWEPT_EDGE",EDGE,{"disambiguationData":[OSD([sQuery(id+"F3.wireOp",EDGE,"E39.2.10"),sQuery(id+"F3.wireOp",EDGE,"E39.2.14")])]})});
            var Q58;
            Q58=makeQuery(id+"F4.boolean.opBoolean","COPY",EDGE,{"derivedFrom":makeQuery(id+"F4.opExtrude","SWEPT_EDGE",EDGE,{"disambiguationData":[OSD([sQuery(id+"F3.wireOp",EDGE,"E39.2.3"),sQuery(id+"F3.wireOp",EDGE,"E39.2.7")])]})});
            var Q59;
            Q59=makeQuery(id+"F4.boolean.opBoolean","COPY",EDGE,{"derivedFrom":makeQuery(id+"F4.opExtrude","SWEPT_EDGE",EDGE,{"disambiguationData":[OSD([sQuery(id+"F3.wireOp",EDGE,"E39.2.1"),sQuery(id+"F3.wireOp",EDGE,"E39.2.6")])]})});
            var Q60;
            Q60=makeQuery(id+"F4.boolean.opBoolean","COPY",EDGE,{"derivedFrom":makeQuery(id+"F4.opExtrude","SWEPT_EDGE",EDGE,{"disambiguationData":[OSD([sQuery(id+"F3.wireOp",EDGE,"E39.2.2"),sQuery(id+"F3.wireOp",EDGE,"E39.2.8")])]})});
            var Q61;
            Q61=makeQuery(id+"F4.boolean.opBoolean","COPY",EDGE,{"derivedFrom":makeQuery(id+"F4.opExtrude","SWEPT_EDGE",EDGE,{"disambiguationData":[OSD([sQuery(id+"F3.wireOp",EDGE,"E39.2.4"),sQuery(id+"F3.wireOp",EDGE,"E39.2.9")])]})});
            var Q62;
            Q62=makeQuery(id+"F4.boolean.opBoolean","COPY",EDGE,{"derivedFrom":makeQuery(id+"F4.opExtrude","SWEPT_EDGE",EDGE,{"disambiguationData":[OSD([sQuery(id+"F3.wireOp",EDGE,"E39.2.0"),sQuery(id+"F3.wireOp",EDGE,"E39.2.5")])]})});
            var Q63;
            Q63=makeQuery(id+"F5.boolean.opBoolean","COPY",EDGE,{"derivedFrom":makeQuery(id+"F5.opExtrude","SWEPT_EDGE",EDGE,{"disambiguationData":[OSD([sQuery(id+"F3.wireOp",EDGE,"E39.2.15"),sQuery(id+"F3.wireOp",EDGE,"E39.2.18")])]})});
            var Q64;
            Q64=makeQuery(id+"F5.boolean.opBoolean","COPY",EDGE,{"derivedFrom":makeQuery(id+"F5.opExtrude","SWEPT_EDGE",EDGE,{"disambiguationData":[OSD([sQuery(id+"F3.wireOp",EDGE,"E39.2.17"),sQuery(id+"F3.wireOp",EDGE,"E39.2.19")])]})});
            var Q65;
            Q65=makeQuery(id+"F5.boolean.opBoolean","COPY",EDGE,{"derivedFrom":makeQuery(id+"F5.opExtrude","SWEPT_EDGE",EDGE,{"disambiguationData":[OSD([sQuery(id+"F3.wireOp",EDGE,"E39.2.21"),sQuery(id+"F3.wireOp",EDGE,"E39.2.22")])]})});
            var Q66;
            Q66=makeQuery(id+"F5.boolean.opBoolean","COPY",EDGE,{"derivedFrom":makeQuery(id+"F5.opExtrude","SWEPT_EDGE",EDGE,{"disambiguationData":[OSD([sQuery(id+"F3.wireOp",EDGE,"E39.2.16"),sQuery(id+"F3.wireOp",EDGE,"E39.2.18")])]})});
            var Q67;
            Q67=makeQuery(id+"F5.boolean.opBoolean","COPY",EDGE,{"derivedFrom":makeQuery(id+"F5.opExtrude","SWEPT_EDGE",EDGE,{"disambiguationData":[OSD([sQuery(id+"F3.wireOp",EDGE,"E39.2.19"),sQuery(id+"F3.wireOp",EDGE,"E39.2.20")])]})});
            var Q68;
            Q68=makeQuery(id+"F5.boolean.opBoolean","COPY",EDGE,{"derivedFrom":makeQuery(id+"F5.opExtrude","SWEPT_EDGE",EDGE,{"disambiguationData":[OSD([sQuery(id+"F3.wireOp",EDGE,"E39.2.22"),sQuery(id+"F3.wireOp",EDGE,"E39.2.23")])]})});
            var Q69;
            Q69=makeQuery(id+"F5.boolean.opBoolean","COPY",EDGE,{"derivedFrom":makeQuery(id+"F5.opExtrude","SWEPT_EDGE",EDGE,{"disambiguationData":[OSD([sQuery(id+"F3.wireOp",EDGE,"E39.1.21"),sQuery(id+"F3.wireOp",EDGE,"E39.1.22")])]})});
            var Q70;
            Q70=makeQuery(id+"F5.boolean.opBoolean","COPY",EDGE,{"derivedFrom":makeQuery(id+"F5.opExtrude","SWEPT_EDGE",EDGE,{"disambiguationData":[OSD([sQuery(id+"F3.wireOp",EDGE,"E39.1.17"),sQuery(id+"F3.wireOp",EDGE,"E39.1.19")])]})});
            var Q71;
            Q71=makeQuery(id+"F5.boolean.opBoolean","COPY",EDGE,{"derivedFrom":makeQuery(id+"F5.opExtrude","SWEPT_EDGE",EDGE,{"disambiguationData":[OSD([sQuery(id+"F3.wireOp",EDGE,"E39.1.15"),sQuery(id+"F3.wireOp",EDGE,"E39.1.18")])]})});
            var Q72;
            Q72=makeQuery(id+"F4.boolean.opBoolean","COPY",EDGE,{"derivedFrom":makeQuery(id+"F4.opExtrude","SWEPT_EDGE",EDGE,{"disambiguationData":[OSD([sQuery(id+"F3.wireOp",EDGE,"E39.1.4"),sQuery(id+"F3.wireOp",EDGE,"E39.1.9")])]})});
            var Q73;
            Q73=makeQuery(id+"F4.boolean.opBoolean","COPY",EDGE,{"derivedFrom":makeQuery(id+"F4.opExtrude","SWEPT_EDGE",EDGE,{"disambiguationData":[OSD([sQuery(id+"F3.wireOp",EDGE,"E39.1.2"),sQuery(id+"F3.wireOp",EDGE,"E39.1.8")])]})});
            var Q74;
            Q74=makeQuery(id+"F4.boolean.opBoolean","COPY",EDGE,{"derivedFrom":makeQuery(id+"F4.opExtrude","SWEPT_EDGE",EDGE,{"disambiguationData":[OSD([sQuery(id+"F3.wireOp",EDGE,"E39.1.0"),sQuery(id+"F3.wireOp",EDGE,"E39.1.5")])]})});
            var Q75;
            Q75=makeQuery(id+"F4.boolean.opBoolean","COPY",EDGE,{"derivedFrom":makeQuery(id+"F4.opExtrude","SWEPT_EDGE",EDGE,{"disambiguationData":[OSD([sQuery(id+"F3.wireOp",EDGE,"E39.1.1"),sQuery(id+"F3.wireOp",EDGE,"E39.1.5")])]})});
            var Q76;
            Q76=makeQuery(id+"F4.boolean.opBoolean","COPY",EDGE,{"derivedFrom":makeQuery(id+"F4.opExtrude","SWEPT_EDGE",EDGE,{"disambiguationData":[OSD([sQuery(id+"F3.wireOp",EDGE,"E39.1.3"),sQuery(id+"F3.wireOp",EDGE,"E39.1.8")])]})});
            var Q77;
            Q77=makeQuery(id+"F4.boolean.opBoolean","COPY",EDGE,{"derivedFrom":makeQuery(id+"F4.opExtrude","SWEPT_EDGE",EDGE,{"disambiguationData":[OSD([sQuery(id+"F3.wireOp",EDGE,"E39.1.9"),sQuery(id+"F3.wireOp",EDGE,"E39.1.14")])]})});
            var Q78;
            Q78=makeQuery(id+"F5.boolean.opBoolean","COPY",EDGE,{"derivedFrom":makeQuery(id+"F5.opExtrude","SWEPT_EDGE",EDGE,{"disambiguationData":[OSD([sQuery(id+"F3.wireOp",EDGE,"E39.1.16"),sQuery(id+"F3.wireOp",EDGE,"E39.1.18")])]})});
            var Q79;
            Q79=makeQuery(id+"F5.boolean.opBoolean","COPY",EDGE,{"derivedFrom":makeQuery(id+"F5.opExtrude","SWEPT_EDGE",EDGE,{"disambiguationData":[OSD([sQuery(id+"F3.wireOp",EDGE,"E39.1.19"),sQuery(id+"F3.wireOp",EDGE,"E39.1.20")])]})});
            var Q80;
            Q80=makeQuery(id+"F5.boolean.opBoolean","COPY",EDGE,{"derivedFrom":makeQuery(id+"F5.opExtrude","SWEPT_EDGE",EDGE,{"disambiguationData":[OSD([sQuery(id+"F3.wireOp",EDGE,"E39.1.22"),sQuery(id+"F3.wireOp",EDGE,"E39.1.23")])]})});
            var Q81;
            Q81=makeQuery(id+"F4.boolean.opBoolean","COPY",EDGE,{"derivedFrom":makeQuery(id+"F4.opExtrude","SWEPT_EDGE",EDGE,{"disambiguationData":[OSD([sQuery(id+"F3.wireOp",EDGE,"E39.1.0"),sQuery(id+"F3.wireOp",EDGE,"E39.1.6")])]})});
            var Q82;
            Q82=makeQuery(id+"F4.boolean.opBoolean","COPY",EDGE,{"derivedFrom":makeQuery(id+"F4.opExtrude","SWEPT_EDGE",EDGE,{"disambiguationData":[OSD([sQuery(id+"F3.wireOp",EDGE,"E39.1.2"),sQuery(id+"F3.wireOp",EDGE,"E39.1.7")])]})});
            var Q83;
            Q83=makeQuery(id+"F4.boolean.opBoolean","COPY",EDGE,{"derivedFrom":makeQuery(id+"F4.opExtrude","SWEPT_EDGE",EDGE,{"disambiguationData":[OSD([sQuery(id+"F3.wireOp",EDGE,"E39.1.4"),sQuery(id+"F3.wireOp",EDGE,"E39.1.10")])]})});
            var Q84;
            Q84=makeQuery(id+"F5.boolean.opBoolean","COPY",EDGE,{"derivedFrom":makeQuery(id+"F5.opExtrude","SWEPT_EDGE",EDGE,{"disambiguationData":[OSD([sQuery(id+"F3.wireOp",EDGE,"E39.1.11"),sQuery(id+"F3.wireOp",EDGE,"E39.1.15")])]})});
            var Q85;
            Q85=makeQuery(id+"F5.boolean.opBoolean","COPY",EDGE,{"derivedFrom":makeQuery(id+"F5.opExtrude","SWEPT_EDGE",EDGE,{"disambiguationData":[OSD([sQuery(id+"F3.wireOp",EDGE,"E39.1.12"),sQuery(id+"F3.wireOp",EDGE,"E39.1.17")])]})});
            var Q86;
            Q86=makeQuery(id+"F5.boolean.opBoolean","COPY",EDGE,{"derivedFrom":makeQuery(id+"F5.opExtrude","SWEPT_EDGE",EDGE,{"disambiguationData":[OSD([sQuery(id+"F3.wireOp",EDGE,"E39.1.13"),sQuery(id+"F3.wireOp",EDGE,"E39.1.21")])]})});
            var Q87;
            Q87=makeQuery(id+"F5.boolean.opBoolean","COPY",EDGE,{"derivedFrom":makeQuery(id+"F5.opExtrude","SWEPT_EDGE",EDGE,{"disambiguationData":[OSD([sQuery(id+"F3.wireOp",EDGE,"E39.1.13"),sQuery(id+"F3.wireOp",EDGE,"E39.1.23")])]})});
            var Q88;
            Q88=makeQuery(id+"F5.boolean.opBoolean","COPY",EDGE,{"derivedFrom":makeQuery(id+"F5.opExtrude","SWEPT_EDGE",EDGE,{"disambiguationData":[OSD([sQuery(id+"F3.wireOp",EDGE,"E39.1.11"),sQuery(id+"F3.wireOp",EDGE,"E39.1.16")])]})});
            var Q89;
            Q89=makeQuery(id+"F4.boolean.opBoolean","COPY",EDGE,{"derivedFrom":makeQuery(id+"F4.opExtrude","SWEPT_EDGE",EDGE,{"disambiguationData":[OSD([sQuery(id+"F3.wireOp",EDGE,"E39.1.10"),sQuery(id+"F3.wireOp",EDGE,"E39.1.14")])]})});
            var Q90;
            Q90=makeQuery(id+"F4.boolean.opBoolean","COPY",EDGE,{"derivedFrom":makeQuery(id+"F4.opExtrude","SWEPT_EDGE",EDGE,{"disambiguationData":[OSD([sQuery(id+"F3.wireOp",EDGE,"E39.1.3"),sQuery(id+"F3.wireOp",EDGE,"E39.1.7")])]})});
            var Q91;
            Q91=makeQuery(id+"F4.boolean.opBoolean","COPY",EDGE,{"derivedFrom":makeQuery(id+"F4.opExtrude","SWEPT_EDGE",EDGE,{"disambiguationData":[OSD([sQuery(id+"F3.wireOp",EDGE,"E39.1.1"),sQuery(id+"F3.wireOp",EDGE,"E39.1.6")])]})});
            var Q92;
            Q92=makeQuery(id+"F5.boolean.opBoolean","COPY",EDGE,{"derivedFrom":makeQuery(id+"F5.opExtrude","SWEPT_EDGE",EDGE,{"disambiguationData":[OSD([sQuery(id+"F3.wireOp",EDGE,"E39.1.12"),sQuery(id+"F3.wireOp",EDGE,"E39.1.20")])]})});
            fillet(context, id + "F6", {"entities" : qUnion([Q0, Q1, Q2, Q3, Q4, Q5, Q6, Q7, Q8, Q9, Q10, Q11, Q12, Q13, Q14, Q15, Q16, Q17, Q18, Q19, Q20, Q21, Q22, Q23, Q24, Q25, Q26, Q27, Q28, Q29, Q30, Q31, Q32, Q33, Q34, Q35, Q36, Q37, Q38, Q39, Q40, Q41, Q42, Q43, Q44, Q45, Q46, Q47, Q48, Q49, Q50, Q51, Q52, Q53, Q54, Q55, Q56, Q57, Q58, Q59, Q60, Q61, Q62, Q63, Q64, Q65, Q66, Q67, Q68, Q69, Q70, Q71, Q72, Q73, Q74, Q75, Q76, Q77, Q78, Q79, Q80, Q81, Q82, Q83, Q84, Q85, Q86, Q87, Q88, Q89, Q90, Q91, Q92]), "radius" : 2 * mm, "tangentPropagation" : true, "allowEdgeOverflow" : false});
        }
    });
